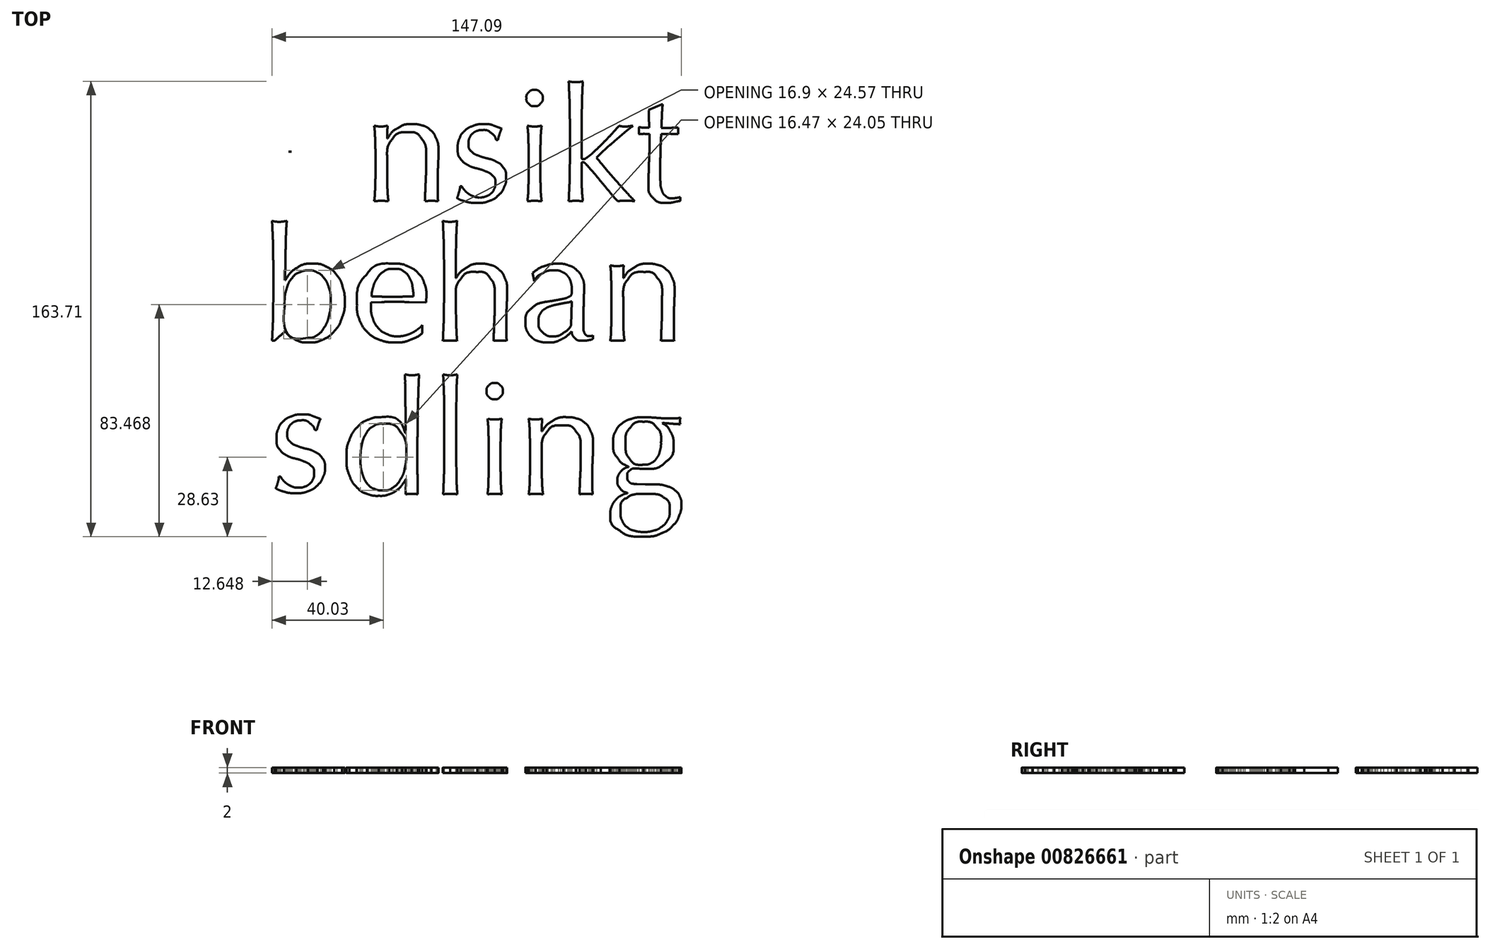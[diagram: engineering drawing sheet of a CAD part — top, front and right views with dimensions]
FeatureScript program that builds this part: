
annotation { "Feature Type Name" : "Feature", "Feature Type Description" : "" }
export const myFeature = defineFeature(function(context is Context, id is Id, definition is map)
    precondition{}
    {
        {
            var Q0;
            Q0=qCreatedBy(makeId("Top.planeOp"),FACE);
            var sketch = newSketch(context, id + "F0", { "sketchPlane" : qUnion([Q0])});
            skFitSpline(sketch, "E0", {"points": [v(-65.69, 52.86) * mm, v(-64.7, 52.86) * mm, v(-63.67, 52.84) * mm, v(-62.6, 52.8) * mm]});
            skFitSpline(sketch, "E1", {"points": [v(-62.6, 52.8) * mm, v(-61.54, 52.76) * mm, v(-60.5, 52.74) * mm, v(-59.52, 52.74) * mm]});
            skFitSpline(sketch, "E2", {"points": [v(-59.52, 52.74) * mm, v(-58.45, 52.74) * mm, v(-57.39, 52.74) * mm, v(-56.32, 52.74) * mm]});
            skFitSpline(sketch, "E3", {"points": [v(-56.32, 52.74) * mm, v(-55.25, 52.78) * mm, v(-54.19, 52.82) * mm, v(-53.12, 52.86) * mm]});
            skFitSpline(sketch, "E4", {"points": [v(-40.38, 35.08) * mm, v(-40.9, 35.16) * mm, v(-41.42, 35.2) * mm, v(-41.92, 35.2) * mm]});
            skFitSpline(sketch, "E5", {"points": [v(-41.92, 35.2) * mm, v(-42.38, 35.2) * mm, v(-42.87, 35.2) * mm, v(-43.4, 35.2) * mm]});
            skFitSpline(sketch, "E6", {"points": [v(-43.4, 35.2) * mm, v(-43.94, 35.2) * mm, v(-44.45, 35.2) * mm, v(-44.95, 35.2) * mm]});
            skFitSpline(sketch, "E7", {"points": [v(-44.95, 35.2) * mm, v(-45.4, 35.2) * mm, v(-45.9, 35.16) * mm, v(-46.43, 35.08) * mm]});
            skFitSpline(sketch, "E8", {"points": [v(-46.43, 35.08) * mm, v(-46.7, 35.96) * mm, v(-47.06, 37) * mm, v(-47.52, 38.23) * mm]});
            skFitSpline(sketch, "E9", {"points": [v(-47.52, 38.23) * mm, v(-47.98, 39.48) * mm, v(-48.49, 40.78) * mm, v(-49.06, 42.11) * mm]});
            skFitSpline(sketch, "E10", {"points": [v(-49.06, 42.11) * mm, v(-49.6, 43.48) * mm, v(-50.15, 44.86) * mm, v(-50.72, 46.23) * mm]});
            skFitSpline(sketch, "E11", {"points": [v(-50.72, 46.23) * mm, v(-51.29, 47.64) * mm, v(-51.82, 48.97) * mm, v(-52.32, 50.23) * mm]});
            skFitSpline(sketch, "E12", {"points": [v(-52.32, 50.23) * mm, v(-53.54, 50.27) * mm, v(-54.78, 50.28) * mm, v(-56.03, 50.28) * mm]});
            skFitSpline(sketch, "E13", {"points": [v(-56.03, 50.28) * mm, v(-57.29, 50.32) * mm, v(-58.55, 50.34) * mm, v(-59.8, 50.34) * mm]});
            skFitSpline(sketch, "E14", {"points": [v(-59.8, 50.34) * mm, v(-60.99, 50.34) * mm, v(-62.15, 50.32) * mm, v(-63.29, 50.28) * mm]});
            skFitSpline(sketch, "E15", {"points": [v(-63.29, 50.28) * mm, v(-64.43, 50.28) * mm, v(-65.6, 50.27) * mm, v(-66.78, 50.23) * mm]});
            skFitSpline(sketch, "E16", {"points": [v(-66.78, 50.23) * mm, v(-68, 47.26) * mm, v(-69.1, 44.42) * mm, v(-70.09, 41.71) * mm]});
            skFitSpline(sketch, "E17", {"points": [v(-70.09, 41.71) * mm, v(-71.08, 39.05) * mm, v(-71.82, 36.84) * mm, v(-72.32, 35.08) * mm]});
            skFitSpline(sketch, "E18", {"points": [v(-72.32, 35.08) * mm, v(-72.97, 35.16) * mm, v(-73.67, 35.2) * mm, v(-74.43, 35.2) * mm]});
            skFitSpline(sketch, "E19", {"points": [v(-74.43, 35.2) * mm, v(-75.2, 35.2) * mm, v(-75.9, 35.16) * mm, v(-76.55, 35.08) * mm]});
            skFitSpline(sketch, "E20", {"points": [v(-76.55, 35.08) * mm, v(-73.46, 41.75) * mm, v(-70.45, 48.38) * mm, v(-67.52, 54.97) * mm]});
            skFitSpline(sketch, "E21", {"points": [v(-67.52, 54.97) * mm, v(-64.59, 61.56) * mm, v(-61.63, 68.27) * mm, v(-58.66, 75.08) * mm]});
            skLineSegment(sketch, "E22", {"start": v(-53.12, 52.86) * mm, "end": v(-59.46, 67.37) * mm});
            skLineSegment(sketch, "E23", {"start": v(-59.46, 67.37) * mm, "end": v(-65.69, 52.86) * mm});
            skLineSegment(sketch, "E24", {"start": v(-65.69, 52.86) * mm, "end": v(-53.12, 52.86) * mm});
            skFitSpline(sketch, "E25", {"points": [v(-57.58, 75.08) * mm, v(-56.66, 72.88) * mm, v(-55.67, 70.48) * mm, v(-54.6, 67.88) * mm]});
            skFitSpline(sketch, "E26", {"points": [v(-54.6, 67.88) * mm, v(-53.54, 65.33) * mm, v(-52.45, 62.74) * mm, v(-51.35, 60.11) * mm]});
            skFitSpline(sketch, "E27", {"points": [v(-51.35, 60.11) * mm, v(-50.24, 57.48) * mm, v(-49.14, 54.88) * mm, v(-48.03, 52.28) * mm]});
            skFitSpline(sketch, "E28", {"points": [v(-48.03, 52.28) * mm, v(-46.93, 49.7) * mm, v(-45.9, 47.28) * mm, v(-44.95, 45.03) * mm]});
            skFitSpline(sketch, "E29", {"points": [v(-44.95, 45.03) * mm, v(-43.96, 42.82) * mm, v(-43.08, 40.84) * mm, v(-42.32, 39.08) * mm]});
            skFitSpline(sketch, "E30", {"points": [v(-42.32, 39.08) * mm, v(-41.52, 37.33) * mm, v(-40.87, 36) * mm, v(-40.38, 35.08) * mm]});
            skLineSegment(sketch, "E31", {"start": v(-58.66, 75.08) * mm, "end": v(-57.58, 75.08) * mm});
            skLineSegment(sketch, "E32", {"start": v(-57.58, 75.08) * mm, "end": v(-58.66, 75.08) * mm});
            skFitSpline(sketch, "E33", {"points": [v(-16.38, 47.66) * mm, v(-16.38, 45.45) * mm, v(-16.43, 43.3) * mm, v(-16.55, 41.2) * mm]});
            skFitSpline(sketch, "E34", {"points": [v(-16.55, 41.2) * mm, v(-16.62, 39.1) * mm, v(-16.7, 37.07) * mm, v(-16.78, 35.08) * mm]});
            skFitSpline(sketch, "E35", {"points": [v(-16.78, 35.08) * mm, v(-16.02, 35.16) * mm, v(-15.23, 35.2) * mm, v(-14.43, 35.2) * mm]});
            skFitSpline(sketch, "E36", {"points": [v(-14.43, 35.2) * mm, v(-13.6, 35.2) * mm, v(-12.8, 35.16) * mm, v(-12.03, 35.08) * mm]});
            skFitSpline(sketch, "E37", {"points": [v(-12.03, 35.08) * mm, v(-12.07, 35.62) * mm, v(-12.11, 36.17) * mm, v(-12.15, 36.74) * mm]});
            skFitSpline(sketch, "E38", {"points": [v(-12.15, 36.74) * mm, v(-12.15, 37.35) * mm, v(-12.15, 37.96) * mm, v(-12.15, 38.57) * mm]});
            skLineSegment(sketch, "E39", {"start": v(-16.38, 51.14) * mm, "end": v(-16.38, 47.66) * mm});
            skLineSegment(sketch, "E40", {"start": v(-16.38, 47.66) * mm, "end": v(-16.38, 51.14) * mm});
            skFitSpline(sketch, "E41", {"points": [v(-12.15, 42.28) * mm, v(-12.15, 44.23) * mm, v(-12.11, 46.06) * mm, v(-12.03, 47.77) * mm]});
            skFitSpline(sketch, "E42", {"points": [v(-12.03, 47.77) * mm, v(-11.96, 49.52) * mm, v(-11.92, 51.22) * mm, v(-11.92, 52.86) * mm]});
            skFitSpline(sketch, "E43", {"points": [v(-11.92, 52.86) * mm, v(-11.92, 54.84) * mm, v(-12.2, 56.46) * mm, v(-12.78, 57.71) * mm]});
            skFitSpline(sketch, "E44", {"points": [v(-12.78, 57.71) * mm, v(-13.31, 59) * mm, v(-14.02, 60.02) * mm, v(-14.9, 60.74) * mm]});
            skFitSpline(sketch, "E45", {"points": [v(-14.9, 60.74) * mm, v(-15.77, 61.5) * mm, v(-16.76, 62.04) * mm, v(-17.86, 62.34) * mm]});
            skFitSpline(sketch, "E46", {"points": [v(-17.86, 62.34) * mm, v(-18.93, 62.65) * mm, v(-20, 62.8) * mm, v(-21.06, 62.8) * mm]});
            skFitSpline(sketch, "E47", {"points": [v(-21.06, 62.8) * mm, v(-23.12, 62.8) * mm, v(-24.9, 62.34) * mm, v(-26.38, 61.43) * mm]});
            skFitSpline(sketch, "E48", {"points": [v(-26.38, 61.43) * mm, v(-27.86, 60.55) * mm, v(-29.14, 59.3) * mm, v(-30.2, 57.66) * mm]});
            skLineSegment(sketch, "E49", {"start": v(-12.15, 38.57) * mm, "end": v(-12.15, 42.28) * mm});
            skLineSegment(sketch, "E50", {"start": v(-12.15, 42.28) * mm, "end": v(-12.15, 38.57) * mm});
            skFitSpline(sketch, "E51", {"points": [v(-30.32, 57.66) * mm, v(-30.32, 59.18) * mm, v(-30.26, 60.7) * mm, v(-30.15, 62.23) * mm]});
            skFitSpline(sketch, "E52", {"points": [v(-30.15, 62.23) * mm, v(-30.64, 62.15) * mm, v(-31.08, 62.08) * mm, v(-31.46, 62) * mm]});
            skFitSpline(sketch, "E53", {"points": [v(-31.46, 62) * mm, v(-31.8, 61.96) * mm, v(-32.13, 61.94) * mm, v(-32.43, 61.94) * mm]});
            skFitSpline(sketch, "E54", {"points": [v(-32.43, 61.94) * mm, v(-33.08, 61.94) * mm, v(-33.94, 62.04) * mm, v(-35, 62.23) * mm]});
            skFitSpline(sketch, "E55", {"points": [v(-35, 62.23) * mm, v(-34.82, 60.59) * mm, v(-34.7, 58.82) * mm, v(-34.66, 56.91) * mm]});
            skFitSpline(sketch, "E56", {"points": [v(-34.66, 56.91) * mm, v(-34.59, 55.05) * mm, v(-34.55, 53.26) * mm, v(-34.55, 51.54) * mm]});
            skLineSegment(sketch, "E57", {"start": v(-30.2, 57.66) * mm, "end": v(-30.32, 57.66) * mm});
            skLineSegment(sketch, "E58", {"start": v(-30.32, 57.66) * mm, "end": v(-30.2, 57.66) * mm});
            skFitSpline(sketch, "E59", {"points": [v(-34.55, 45.6) * mm, v(-34.55, 43.88) * mm, v(-34.59, 42.08) * mm, v(-34.66, 40.17) * mm]});
            skFitSpline(sketch, "E60", {"points": [v(-34.66, 40.17) * mm, v(-34.7, 38.3) * mm, v(-34.82, 36.6) * mm, v(-35, 35.08) * mm]});
            skFitSpline(sketch, "E61", {"points": [v(-35, 35.08) * mm, v(-34.13, 35.16) * mm, v(-33.27, 35.2) * mm, v(-32.43, 35.2) * mm]});
            skFitSpline(sketch, "E62", {"points": [v(-32.43, 35.2) * mm, v(-31.6, 35.2) * mm, v(-30.74, 35.16) * mm, v(-29.86, 35.08) * mm]});
            skFitSpline(sketch, "E63", {"points": [v(-29.86, 35.08) * mm, v(-30.05, 36.6) * mm, v(-30.19, 38.3) * mm, v(-30.26, 40.17) * mm]});
            skFitSpline(sketch, "E64", {"points": [v(-30.26, 40.17) * mm, v(-30.3, 42.08) * mm, v(-30.32, 43.88) * mm, v(-30.32, 45.6) * mm]});
            skLineSegment(sketch, "E65", {"start": v(-34.55, 51.54) * mm, "end": v(-34.55, 45.6) * mm});
            skLineSegment(sketch, "E66", {"start": v(-34.55, 45.6) * mm, "end": v(-34.55, 51.54) * mm});
            skFitSpline(sketch, "E67", {"points": [v(-30.32, 50.46) * mm, v(-30.32, 53.43) * mm, v(-29.71, 55.73) * mm, v(-28.5, 57.37) * mm]});
            skFitSpline(sketch, "E68", {"points": [v(-28.5, 57.37) * mm, v(-27.23, 59) * mm, v(-25.27, 59.83) * mm, v(-22.6, 59.83) * mm]});
            skFitSpline(sketch, "E69", {"points": [v(-22.6, 59.83) * mm, v(-20.66, 59.83) * mm, v(-19.14, 59.08) * mm, v(-18.03, 57.6) * mm]});
            skFitSpline(sketch, "E70", {"points": [v(-18.03, 57.6) * mm, v(-16.93, 56.15) * mm, v(-16.38, 54) * mm, v(-16.38, 51.14) * mm]});
            skLineSegment(sketch, "E71", {"start": v(-30.32, 45.6) * mm, "end": v(-30.32, 50.46) * mm});
            skLineSegment(sketch, "E72", {"start": v(-30.32, 50.46) * mm, "end": v(-30.32, 45.6) * mm});
            skFitSpline(sketch, "E73", {"points": [v(-4.17, 40.4) * mm, v(-4.17, 39.83) * mm, v(-4.3, 39.1) * mm, v(-4.57, 38.23) * mm]});
            skFitSpline(sketch, "E74", {"points": [v(-4.57, 38.23) * mm, v(-4.8, 37.39) * mm, v(-5.03, 36.72) * mm, v(-5.26, 36.23) * mm]});
            skFitSpline(sketch, "E75", {"points": [v(-5.26, 36.23) * mm, v(-4.46, 35.77) * mm, v(-3.46, 35.37) * mm, v(-2.28, 35.03) * mm]});
            skFitSpline(sketch, "E76", {"points": [v(-2.28, 35.03) * mm, v(-1.1, 34.68) * mm, v(0.36, 34.51) * mm, v(2.12, 34.51) * mm]});
            skFitSpline(sketch, "E77", {"points": [v(2.12, 34.51) * mm, v(3.72, 34.51) * mm, v(5.14, 34.74) * mm, v(6.4, 35.2) * mm]});
            skFitSpline(sketch, "E78", {"points": [v(6.4, 35.2) * mm, v(7.66, 35.7) * mm, v(8.73, 36.36) * mm, v(9.6, 37.2) * mm]});
            skFitSpline(sketch, "E79", {"points": [v(9.6, 37.2) * mm, v(10.52, 38.08) * mm, v(11.2, 39.05) * mm, v(11.66, 40.11) * mm]});
            skFitSpline(sketch, "E80", {"points": [v(11.66, 40.11) * mm, v(12.15, 41.18) * mm, v(12.4, 42.27) * mm, v(12.4, 43.37) * mm]});
            skFitSpline(sketch, "E81", {"points": [v(12.4, 43.37) * mm, v(12.4, 44.97) * mm, v(12.06, 46.23) * mm, v(11.37, 47.14) * mm]});
            skFitSpline(sketch, "E82", {"points": [v(11.37, 47.14) * mm, v(10.73, 48.06) * mm, v(9.9, 48.76) * mm, v(8.92, 49.26) * mm]});
            skFitSpline(sketch, "E83", {"points": [v(8.92, 49.26) * mm, v(7.93, 49.79) * mm, v(6.84, 50.19) * mm, v(5.66, 50.46) * mm]});
            skFitSpline(sketch, "E84", {"points": [v(5.66, 50.46) * mm, v(4.48, 50.76) * mm, v(3.4, 51.1) * mm, v(2.4, 51.48) * mm]});
            skFitSpline(sketch, "E85", {"points": [v(2.4, 51.48) * mm, v(1.41, 51.87) * mm, v(0.57, 52.38) * mm, v(-0.11, 53.03) * mm]});
            skFitSpline(sketch, "E86", {"points": [v(-0.11, 53.03) * mm, v(-0.76, 53.71) * mm, v(-1.08, 54.67) * mm, v(-1.08, 55.88) * mm]});
            skFitSpline(sketch, "E87", {"points": [v(-1.08, 55.88) * mm, v(-1.08, 56.72) * mm, v(-0.93, 57.45) * mm, v(-0.63, 58.06) * mm]});
            skFitSpline(sketch, "E88", {"points": [v(-0.63, 58.06) * mm, v(-0.32, 58.67) * mm, v(0.06, 59.16) * mm, v(0.52, 59.54) * mm]});
            skFitSpline(sketch, "E89", {"points": [v(0.52, 59.54) * mm, v(0.97, 59.92) * mm, v(1.49, 60.2) * mm, v(2.06, 60.4) * mm]});
            skFitSpline(sketch, "E90", {"points": [v(2.06, 60.4) * mm, v(2.63, 60.59) * mm, v(3.2, 60.68) * mm, v(3.77, 60.68) * mm]});
            skFitSpline(sketch, "E91", {"points": [v(3.77, 60.68) * mm, v(5.07, 60.68) * mm, v(6.15, 60.32) * mm, v(7.03, 59.6) * mm]});
            skFitSpline(sketch, "E92", {"points": [v(7.03, 59.6) * mm, v(7.9, 58.88) * mm, v(8.5, 58.06) * mm, v(8.8, 57.14) * mm]});
            skLineSegment(sketch, "E93", {"start": v(-3.48, 40.4) * mm, "end": v(-4.17, 40.4) * mm});
            skLineSegment(sketch, "E94", {"start": v(-4.17, 40.4) * mm, "end": v(-3.48, 40.4) * mm});
            skFitSpline(sketch, "E95", {"points": [v(9.49, 57.14) * mm, v(9.56, 57.6) * mm, v(9.74, 58.25) * mm, v(10, 59.08) * mm]});
            skFitSpline(sketch, "E96", {"points": [v(10, 59.08) * mm, v(10.27, 59.92) * mm, v(10.55, 60.63) * mm, v(10.86, 61.2) * mm]});
            skFitSpline(sketch, "E97", {"points": [v(10.86, 61.2) * mm, v(9.98, 61.5) * mm, v(9.05, 61.85) * mm, v(8.06, 62.23) * mm]});
            skFitSpline(sketch, "E98", {"points": [v(8.06, 62.23) * mm, v(7.1, 62.6) * mm, v(5.93, 62.8) * mm, v(4.52, 62.8) * mm]});
            skFitSpline(sketch, "E99", {"points": [v(4.52, 62.8) * mm, v(3, 62.8) * mm, v(1.64, 62.57) * mm, v(0.46, 62.11) * mm]});
            skFitSpline(sketch, "E100", {"points": [v(0.46, 62.11) * mm, v(-0.72, 61.7) * mm, v(-1.71, 61.1) * mm, v(-2.51, 60.34) * mm]});
            skFitSpline(sketch, "E101", {"points": [v(-2.51, 60.34) * mm, v(-3.31, 59.58) * mm, v(-3.92, 58.67) * mm, v(-4.34, 57.6) * mm]});
            skFitSpline(sketch, "E102", {"points": [v(-4.34, 57.6) * mm, v(-4.76, 56.57) * mm, v(-4.97, 55.43) * mm, v(-4.97, 54.17) * mm]});
            skFitSpline(sketch, "E103", {"points": [v(-4.97, 54.17) * mm, v(-4.97, 52.57) * mm, v(-4.65, 51.31) * mm, v(-4, 50.4) * mm]});
            skFitSpline(sketch, "E104", {"points": [v(-4, 50.4) * mm, v(-3.31, 49.48) * mm, v(-2.47, 48.74) * mm, v(-1.48, 48.17) * mm]});
            skFitSpline(sketch, "E105", {"points": [v(-1.48, 48.17) * mm, v(-0.5, 47.64) * mm, v(0.6, 47.22) * mm, v(1.77, 46.91) * mm]});
            skFitSpline(sketch, "E106", {"points": [v(1.77, 46.91) * mm, v(2.95, 46.6) * mm, v(4.04, 46.25) * mm, v(5.03, 45.83) * mm]});
            skFitSpline(sketch, "E107", {"points": [v(5.03, 45.83) * mm, v(6.02, 45.45) * mm, v(6.84, 44.93) * mm, v(7.49, 44.28) * mm]});
            skFitSpline(sketch, "E108", {"points": [v(7.49, 44.28) * mm, v(8.17, 43.68) * mm, v(8.52, 42.78) * mm, v(8.52, 41.6) * mm]});
            skFitSpline(sketch, "E109", {"points": [v(8.52, 41.6) * mm, v(8.52, 40.76) * mm, v(8.36, 40.02) * mm, v(8.06, 39.37) * mm]});
            skFitSpline(sketch, "E110", {"points": [v(8.06, 39.37) * mm, v(7.75, 38.72) * mm, v(7.34, 38.19) * mm, v(6.8, 37.77) * mm]});
            skFitSpline(sketch, "E111", {"points": [v(6.8, 37.77) * mm, v(6.3, 37.35) * mm, v(5.72, 37.03) * mm, v(5.03, 36.8) * mm]});
            skFitSpline(sketch, "E112", {"points": [v(5.03, 36.8) * mm, v(4.38, 36.57) * mm, v(3.7, 36.46) * mm, v(2.97, 36.46) * mm]});
            skFitSpline(sketch, "E113", {"points": [v(2.97, 36.46) * mm, v(2.17, 36.46) * mm, v(1.41, 36.59) * mm, v(0.69, 36.86) * mm]});
            skFitSpline(sketch, "E114", {"points": [v(0.69, 36.86) * mm, v(0, 37.12) * mm, v(-0.63, 37.45) * mm, v(-1.2, 37.83) * mm]});
            skFitSpline(sketch, "E115", {"points": [v(-1.2, 37.83) * mm, v(-1.73, 38.25) * mm, v(-2.2, 38.68) * mm, v(-2.63, 39.14) * mm]});
            skFitSpline(sketch, "E116", {"points": [v(-2.63, 39.14) * mm, v(-3, 39.6) * mm, v(-3.3, 40.02) * mm, v(-3.48, 40.4) * mm]});
            skLineSegment(sketch, "E117", {"start": v(8.8, 57.14) * mm, "end": v(9.49, 57.14) * mm});
            skLineSegment(sketch, "E118", {"start": v(9.49, 57.14) * mm, "end": v(8.8, 57.14) * mm});
            skFitSpline(sketch, "E119", {"points": [v(19.7, 72.17) * mm, v(19.7, 71.37) * mm, v(19.98, 70.68) * mm, v(20.55, 70.11) * mm]});
            skFitSpline(sketch, "E120", {"points": [v(20.55, 70.11) * mm, v(21.13, 69.54) * mm, v(21.81, 69.26) * mm, v(22.61, 69.26) * mm]});
            skFitSpline(sketch, "E121", {"points": [v(22.61, 69.26) * mm, v(23.41, 69.26) * mm, v(24.1, 69.54) * mm, v(24.67, 70.11) * mm]});
            skFitSpline(sketch, "E122", {"points": [v(24.67, 70.11) * mm, v(25.24, 70.68) * mm, v(25.53, 71.37) * mm, v(25.53, 72.17) * mm]});
            skFitSpline(sketch, "E123", {"points": [v(25.53, 72.17) * mm, v(25.53, 72.97) * mm, v(25.24, 73.66) * mm, v(24.67, 74.23) * mm]});
            skFitSpline(sketch, "E124", {"points": [v(24.67, 74.23) * mm, v(24.1, 74.8) * mm, v(23.41, 75.08) * mm, v(22.61, 75.08) * mm]});
            skFitSpline(sketch, "E125", {"points": [v(22.61, 75.08) * mm, v(21.81, 75.08) * mm, v(21.13, 74.8) * mm, v(20.55, 74.23) * mm]});
            skFitSpline(sketch, "E126", {"points": [v(20.55, 74.23) * mm, v(19.98, 73.66) * mm, v(19.7, 72.97) * mm, v(19.7, 72.17) * mm]});
            skFitSpline(sketch, "E127", {"points": [v(20.5, 45.6) * mm, v(20.5, 43.88) * mm, v(20.46, 42.08) * mm, v(20.38, 40.17) * mm]});
            skFitSpline(sketch, "E128", {"points": [v(20.38, 40.17) * mm, v(20.35, 38.3) * mm, v(20.23, 36.6) * mm, v(20.04, 35.08) * mm]});
            skFitSpline(sketch, "E129", {"points": [v(20.04, 35.08) * mm, v(20.92, 35.16) * mm, v(21.77, 35.2) * mm, v(22.61, 35.2) * mm]});
            skFitSpline(sketch, "E130", {"points": [v(22.61, 35.2) * mm, v(23.45, 35.2) * mm, v(24.3, 35.16) * mm, v(25.18, 35.08) * mm]});
            skFitSpline(sketch, "E131", {"points": [v(25.18, 35.08) * mm, v(25, 36.6) * mm, v(24.86, 38.3) * mm, v(24.78, 40.17) * mm]});
            skFitSpline(sketch, "E132", {"points": [v(24.78, 40.17) * mm, v(24.75, 42.08) * mm, v(24.73, 43.88) * mm, v(24.73, 45.6) * mm]});
            skLineSegment(sketch, "E133", {"start": v(20.5, 51.54) * mm, "end": v(20.5, 45.6) * mm});
            skLineSegment(sketch, "E134", {"start": v(20.5, 45.6) * mm, "end": v(20.5, 51.54) * mm});
            skFitSpline(sketch, "E135", {"points": [v(24.73, 51.54) * mm, v(24.73, 53.26) * mm, v(24.75, 55.05) * mm, v(24.78, 56.91) * mm]});
            skFitSpline(sketch, "E136", {"points": [v(24.78, 56.91) * mm, v(24.86, 58.82) * mm, v(25, 60.59) * mm, v(25.18, 62.23) * mm]});
            skFitSpline(sketch, "E137", {"points": [v(25.18, 62.23) * mm, v(24.12, 62.04) * mm, v(23.26, 61.94) * mm, v(22.61, 61.94) * mm]});
            skFitSpline(sketch, "E138", {"points": [v(22.61, 61.94) * mm, v(21.96, 61.94) * mm, v(21.1, 62.04) * mm, v(20.04, 62.23) * mm]});
            skFitSpline(sketch, "E139", {"points": [v(20.04, 62.23) * mm, v(20.23, 60.59) * mm, v(20.35, 58.82) * mm, v(20.38, 56.91) * mm]});
            skFitSpline(sketch, "E140", {"points": [v(20.38, 56.91) * mm, v(20.46, 55.05) * mm, v(20.5, 53.26) * mm, v(20.5, 51.54) * mm]});
            skLineSegment(sketch, "E141", {"start": v(24.73, 45.6) * mm, "end": v(24.73, 51.54) * mm});
            skLineSegment(sketch, "E142", {"start": v(24.73, 51.54) * mm, "end": v(24.73, 45.6) * mm});
            skFitSpline(sketch, "E143", {"points": [v(35.32, 51.37) * mm, v(35.32, 50.08) * mm, v(35.3, 48.67) * mm, v(35.26, 47.14) * mm]});
            skFitSpline(sketch, "E144", {"points": [v(35.26, 47.14) * mm, v(35.26, 45.62) * mm, v(35.24, 44.11) * mm, v(35.2, 42.63) * mm]});
            skFitSpline(sketch, "E145", {"points": [v(35.2, 42.63) * mm, v(35.16, 41.14) * mm, v(35.1, 39.73) * mm, v(35.03, 38.4) * mm]});
            skFitSpline(sketch, "E146", {"points": [v(35.03, 38.4) * mm, v(35, 37.07) * mm, v(34.94, 35.96) * mm, v(34.86, 35.08) * mm]});
            skFitSpline(sketch, "E147", {"points": [v(34.86, 35.08) * mm, v(35.74, 35.16) * mm, v(36.6, 35.2) * mm, v(37.43, 35.2) * mm]});
            skFitSpline(sketch, "E148", {"points": [v(37.43, 35.2) * mm, v(38.27, 35.2) * mm, v(39.13, 35.16) * mm, v(40, 35.08) * mm]});
            skFitSpline(sketch, "E149", {"points": [v(40, 35.08) * mm, v(39.81, 36.72) * mm, v(39.68, 38.34) * mm, v(39.6, 39.94) * mm]});
            skFitSpline(sketch, "E150", {"points": [v(39.6, 39.94) * mm, v(39.56, 41.58) * mm, v(39.55, 43.26) * mm, v(39.55, 44.97) * mm]});
            skLineSegment(sketch, "E151", {"start": v(35.32, 61.71) * mm, "end": v(35.32, 51.37) * mm});
            skLineSegment(sketch, "E152", {"start": v(35.32, 51.37) * mm, "end": v(35.32, 61.71) * mm});
            skFitSpline(sketch, "E153", {"points": [v(39.55, 48.4) * mm, v(39.55, 48.86) * mm, v(39.74, 49.08) * mm, v(40.12, 49.08) * mm]});
            skFitSpline(sketch, "E154", {"points": [v(40.12, 49.08) * mm, v(40.27, 49.08) * mm, v(40.42, 49.03) * mm, v(40.57, 48.91) * mm]});
            skFitSpline(sketch, "E155", {"points": [v(40.57, 48.91) * mm, v(40.73, 48.8) * mm, v(40.86, 48.67) * mm, v(40.97, 48.51) * mm]});
            skFitSpline(sketch, "E156", {"points": [v(40.97, 48.51) * mm, v(41.66, 47.79) * mm, v(42.48, 46.88) * mm, v(43.43, 45.77) * mm]});
            skFitSpline(sketch, "E157", {"points": [v(43.43, 45.77) * mm, v(44.38, 44.67) * mm, v(45.37, 43.48) * mm, v(46.4, 42.23) * mm]});
            skFitSpline(sketch, "E158", {"points": [v(46.4, 42.23) * mm, v(47.47, 40.97) * mm, v(48.54, 39.7) * mm, v(49.6, 38.4) * mm]});
            skFitSpline(sketch, "E159", {"points": [v(49.6, 38.4) * mm, v(50.67, 37.14) * mm, v(51.62, 36.04) * mm, v(52.46, 35.08) * mm]});
            skFitSpline(sketch, "E160", {"points": [v(52.46, 35.08) * mm, v(53, 35.16) * mm, v(53.5, 35.2) * mm, v(54, 35.2) * mm]});
            skFitSpline(sketch, "E161", {"points": [v(54, 35.2) * mm, v(54.5, 35.2) * mm, v(54.96, 35.2) * mm, v(55.37, 35.2) * mm]});
            skFitSpline(sketch, "E162", {"points": [v(55.37, 35.2) * mm, v(55.87, 35.2) * mm, v(56.36, 35.2) * mm, v(56.86, 35.2) * mm]});
            skFitSpline(sketch, "E163", {"points": [v(56.86, 35.2) * mm, v(57.4, 35.2) * mm, v(57.98, 35.16) * mm, v(58.63, 35.08) * mm]});
            skFitSpline(sketch, "E164", {"points": [v(58.63, 35.08) * mm, v(56.23, 37.64) * mm, v(53.87, 40.23) * mm, v(51.55, 42.86) * mm]});
            skFitSpline(sketch, "E165", {"points": [v(51.55, 42.86) * mm, v(49.26, 45.48) * mm, v(47.03, 48.11) * mm, v(44.86, 50.74) * mm]});
            skFitSpline(sketch, "E166", {"points": [v(44.86, 50.74) * mm, v(46.84, 52.68) * mm, v(48.92, 54.59) * mm, v(51.09, 56.46) * mm]});
            skFitSpline(sketch, "E167", {"points": [v(51.09, 56.46) * mm, v(53.3, 58.36) * mm, v(55.6, 60.28) * mm, v(58, 62.23) * mm]});
            skFitSpline(sketch, "E168", {"points": [v(58, 62.23) * mm, v(57.36, 62.15) * mm, v(56.82, 62.08) * mm, v(56.4, 62) * mm]});
            skFitSpline(sketch, "E169", {"points": [v(56.4, 62) * mm, v(55.98, 61.96) * mm, v(55.56, 61.94) * mm, v(55.15, 61.94) * mm]});
            skFitSpline(sketch, "E170", {"points": [v(55.15, 61.94) * mm, v(54.46, 61.94) * mm, v(53.74, 62.04) * mm, v(52.97, 62.23) * mm]});
            skFitSpline(sketch, "E171", {"points": [v(52.97, 62.23) * mm, v(52.1, 61.2) * mm, v(51.13, 60.11) * mm, v(50.06, 58.97) * mm]});
            skFitSpline(sketch, "E172", {"points": [v(50.06, 58.97) * mm, v(49, 57.83) * mm, v(47.95, 56.74) * mm, v(46.92, 55.71) * mm]});
            skFitSpline(sketch, "E173", {"points": [v(46.92, 55.71) * mm, v(45.93, 54.72) * mm, v(45.01, 53.85) * mm, v(44.17, 53.08) * mm]});
            skFitSpline(sketch, "E174", {"points": [v(44.17, 53.08) * mm, v(43.37, 52.32) * mm, v(42.8, 51.8) * mm, v(42.46, 51.54) * mm]});
            skFitSpline(sketch, "E175", {"points": [v(42.46, 51.54) * mm, v(42, 51.2) * mm, v(41.58, 50.9) * mm, v(41.2, 50.63) * mm]});
            skFitSpline(sketch, "E176", {"points": [v(41.2, 50.63) * mm, v(40.86, 50.36) * mm, v(40.54, 50.23) * mm, v(40.23, 50.23) * mm]});
            skFitSpline(sketch, "E177", {"points": [v(40.23, 50.23) * mm, v(39.77, 50.23) * mm, v(39.55, 50.59) * mm, v(39.55, 51.31) * mm]});
            skLineSegment(sketch, "E178", {"start": v(39.55, 44.97) * mm, "end": v(39.55, 48.4) * mm});
            skLineSegment(sketch, "E179", {"start": v(39.55, 48.4) * mm, "end": v(39.55, 44.97) * mm});
            skFitSpline(sketch, "E180", {"points": [v(39.55, 61.71) * mm, v(39.55, 63) * mm, v(39.55, 64.42) * mm, v(39.55, 65.94) * mm]});
            skFitSpline(sketch, "E181", {"points": [v(39.55, 65.94) * mm, v(39.58, 67.47) * mm, v(39.62, 68.97) * mm, v(39.66, 70.46) * mm]});
            skFitSpline(sketch, "E182", {"points": [v(39.66, 70.46) * mm, v(39.7, 71.94) * mm, v(39.74, 73.35) * mm, v(39.77, 74.68) * mm]});
            skFitSpline(sketch, "E183", {"points": [v(39.77, 74.68) * mm, v(39.85, 76.06) * mm, v(39.93, 77.22) * mm, v(40, 78.17) * mm]});
            skFitSpline(sketch, "E184", {"points": [v(40, 78.17) * mm, v(38.94, 77.98) * mm, v(38.08, 77.88) * mm, v(37.43, 77.88) * mm]});
            skFitSpline(sketch, "E185", {"points": [v(37.43, 77.88) * mm, v(36.78, 77.88) * mm, v(35.93, 77.98) * mm, v(34.86, 78.17) * mm]});
            skFitSpline(sketch, "E186", {"points": [v(34.86, 78.17) * mm, v(34.94, 77.22) * mm, v(35, 76.06) * mm, v(35.03, 74.68) * mm]});
            skFitSpline(sketch, "E187", {"points": [v(35.03, 74.68) * mm, v(35.1, 73.35) * mm, v(35.16, 71.94) * mm, v(35.2, 70.46) * mm]});
            skFitSpline(sketch, "E188", {"points": [v(35.2, 70.46) * mm, v(35.24, 68.97) * mm, v(35.26, 67.47) * mm, v(35.26, 65.94) * mm]});
            skFitSpline(sketch, "E189", {"points": [v(35.26, 65.94) * mm, v(35.3, 64.42) * mm, v(35.32, 63) * mm, v(35.32, 61.71) * mm]});
            skLineSegment(sketch, "E190", {"start": v(39.55, 51.31) * mm, "end": v(39.55, 61.71) * mm});
            skLineSegment(sketch, "E191", {"start": v(39.55, 61.71) * mm, "end": v(39.55, 51.31) * mm});
            skFitSpline(sketch, "E192", {"points": [v(63.6, 67.88) * mm, v(63.68, 66.67) * mm, v(63.72, 65.48) * mm, v(63.72, 64.34) * mm]});
            skFitSpline(sketch, "E193", {"points": [v(63.72, 64.34) * mm, v(63.76, 63.2) * mm, v(63.8, 62.25) * mm, v(63.83, 61.48) * mm]});
            skFitSpline(sketch, "E194", {"points": [v(63.83, 61.48) * mm, v(63.03, 61.48) * mm, v(61.77, 61.54) * mm, v(60.06, 61.66) * mm]});
            skFitSpline(sketch, "E195", {"points": [v(60.06, 61.66) * mm, v(60.1, 61.47) * mm, v(60.12, 61.28) * mm, v(60.12, 61.08) * mm]});
            skFitSpline(sketch, "E196", {"points": [v(60.12, 61.08) * mm, v(60.16, 60.9) * mm, v(60.17, 60.7) * mm, v(60.17, 60.51) * mm]});
            skFitSpline(sketch, "E197", {"points": [v(60.17, 60.51) * mm, v(60.17, 60.28) * mm, v(60.16, 60.06) * mm, v(60.12, 59.83) * mm]});
            skFitSpline(sketch, "E198", {"points": [v(60.12, 59.83) * mm, v(60.12, 59.64) * mm, v(60.1, 59.43) * mm, v(60.06, 59.2) * mm]});
            skFitSpline(sketch, "E199", {"points": [v(60.06, 59.2) * mm, v(60.44, 59.24) * mm, v(60.8, 59.26) * mm, v(61.15, 59.26) * mm]});
            skFitSpline(sketch, "E200", {"points": [v(61.15, 59.26) * mm, v(61.49, 59.3) * mm, v(61.81, 59.31) * mm, v(62.12, 59.31) * mm]});
            skLineSegment(sketch, "E201", {"start": v(68.35, 69.88) * mm, "end": v(63.6, 67.88) * mm});
            skLineSegment(sketch, "E202", {"start": v(63.6, 67.88) * mm, "end": v(68.35, 69.88) * mm});
            skFitSpline(sketch, "E203", {"points": [v(63.95, 59.31) * mm, v(63.95, 57.18) * mm, v(63.93, 55.24) * mm, v(63.89, 53.48) * mm]});
            skFitSpline(sketch, "E204", {"points": [v(63.89, 53.48) * mm, v(63.85, 51.77) * mm, v(63.8, 50.19) * mm, v(63.72, 48.74) * mm]});
            skFitSpline(sketch, "E205", {"points": [v(63.72, 48.74) * mm, v(63.68, 47.33) * mm, v(63.64, 46.02) * mm, v(63.6, 44.8) * mm]});
            skFitSpline(sketch, "E206", {"points": [v(63.6, 44.8) * mm, v(63.56, 43.62) * mm, v(63.55, 42.51) * mm, v(63.55, 41.48) * mm]});
            skFitSpline(sketch, "E207", {"points": [v(63.55, 41.48) * mm, v(63.55, 39.2) * mm, v(64.12, 37.47) * mm, v(65.26, 36.28) * mm]});
            skFitSpline(sketch, "E208", {"points": [v(65.26, 36.28) * mm, v(66.4, 35.1) * mm, v(68.17, 34.51) * mm, v(70.57, 34.51) * mm]});
            skFitSpline(sketch, "E209", {"points": [v(70.57, 34.51) * mm, v(71.3, 34.51) * mm, v(72.04, 34.6) * mm, v(72.8, 34.8) * mm]});
            skFitSpline(sketch, "E210", {"points": [v(72.8, 34.8) * mm, v(73.6, 34.95) * mm, v(74.33, 35.08) * mm, v(74.97, 35.2) * mm]});
            skLineSegment(sketch, "E211", {"start": v(62.12, 59.31) * mm, "end": v(63.95, 59.31) * mm});
            skLineSegment(sketch, "E212", {"start": v(63.95, 59.31) * mm, "end": v(62.12, 59.31) * mm});
            skFitSpline(sketch, "E213", {"points": [v(74.97, 36.57) * mm, v(74.6, 36.46) * mm, v(74.14, 36.36) * mm, v(73.6, 36.28) * mm]});
            skFitSpline(sketch, "E214", {"points": [v(73.6, 36.28) * mm, v(73.1, 36.2) * mm, v(72.7, 36.17) * mm, v(72.4, 36.17) * mm]});
            skFitSpline(sketch, "E215", {"points": [v(72.4, 36.17) * mm, v(71.26, 36.17) * mm, v(70.38, 36.42) * mm, v(69.77, 36.91) * mm]});
            skFitSpline(sketch, "E216", {"points": [v(69.77, 36.91) * mm, v(69.16, 37.4) * mm, v(68.7, 38.06) * mm, v(68.4, 38.86) * mm]});
            skFitSpline(sketch, "E217", {"points": [v(68.4, 38.86) * mm, v(68.1, 39.7) * mm, v(67.9, 40.63) * mm, v(67.83, 41.66) * mm]});
            skFitSpline(sketch, "E218", {"points": [v(67.83, 41.66) * mm, v(67.8, 42.68) * mm, v(67.77, 43.73) * mm, v(67.77, 44.8) * mm]});
            skFitSpline(sketch, "E219", {"points": [v(67.77, 44.8) * mm, v(67.77, 46.06) * mm, v(67.77, 47.48) * mm, v(67.77, 49.08) * mm]});
            skFitSpline(sketch, "E220", {"points": [v(67.77, 49.08) * mm, v(67.81, 50.68) * mm, v(67.85, 52.2) * mm, v(67.89, 53.66) * mm]});
            skFitSpline(sketch, "E221", {"points": [v(67.89, 53.66) * mm, v(67.93, 55.14) * mm, v(67.96, 56.42) * mm, v(68, 57.48) * mm]});
            skFitSpline(sketch, "E222", {"points": [v(68, 57.48) * mm, v(68.08, 58.55) * mm, v(68.14, 59.16) * mm, v(68.17, 59.31) * mm]});
            skLineSegment(sketch, "E223", {"start": v(74.97, 35.2) * mm, "end": v(74.97, 36.57) * mm});
            skLineSegment(sketch, "E224", {"start": v(74.97, 36.57) * mm, "end": v(74.97, 35.2) * mm});
            skFitSpline(sketch, "E225", {"points": [v(70.97, 59.31) * mm, v(71.58, 59.31) * mm, v(72.16, 59.3) * mm, v(72.69, 59.26) * mm]});
            skFitSpline(sketch, "E226", {"points": [v(72.69, 59.26) * mm, v(73.22, 59.26) * mm, v(73.74, 59.24) * mm, v(74.23, 59.2) * mm]});
            skFitSpline(sketch, "E227", {"points": [v(74.23, 59.2) * mm, v(74.2, 59.31) * mm, v(74.17, 59.5) * mm, v(74.17, 59.77) * mm]});
            skLineSegment(sketch, "E228", {"start": v(68.17, 59.31) * mm, "end": v(70.97, 59.31) * mm});
            skLineSegment(sketch, "E229", {"start": v(70.97, 59.31) * mm, "end": v(68.17, 59.31) * mm});
            skFitSpline(sketch, "E230", {"points": [v(74.17, 60.97) * mm, v(74.17, 61.28) * mm, v(74.2, 61.48) * mm, v(74.23, 61.6) * mm]});
            skFitSpline(sketch, "E231", {"points": [v(74.23, 61.6) * mm, v(72.9, 61.52) * mm, v(71.66, 61.47) * mm, v(70.52, 61.43) * mm]});
            skFitSpline(sketch, "E232", {"points": [v(70.52, 61.43) * mm, v(69.37, 61.43) * mm, v(68.6, 61.43) * mm, v(68.17, 61.43) * mm]});
            skFitSpline(sketch, "E233", {"points": [v(68.17, 61.43) * mm, v(68.25, 62.84) * mm, v(68.3, 64.23) * mm, v(68.35, 65.6) * mm]});
            skFitSpline(sketch, "E234", {"points": [v(68.35, 65.6) * mm, v(68.42, 67) * mm, v(68.52, 68.44) * mm, v(68.63, 69.88) * mm]});
            skLineSegment(sketch, "E235", {"start": v(74.17, 59.77) * mm, "end": v(74.17, 60.4) * mm});
            skLineSegment(sketch, "E236", {"start": v(74.17, 60.4) * mm, "end": v(74.17, 60.97) * mm});
            skLineSegment(sketch, "E237", {"start": v(74.17, 60.97) * mm, "end": v(74.17, 59.77) * mm});
            skLineSegment(sketch, "E238", {"start": v(68.63, 69.88) * mm, "end": v(68.35, 69.88) * mm});
            skLineSegment(sketch, "E239", {"start": v(68.35, 69.88) * mm, "end": v(68.63, 69.88) * mm});
            skFitSpline(sketch, "E240", {"points": [v(-69.27, -63.98) * mm, v(-69.27, -64.55) * mm, v(-69.4, -65.27) * mm, v(-69.67, -66.15) * mm]});
            skFitSpline(sketch, "E241", {"points": [v(-69.67, -66.15) * mm, v(-69.9, -66.99) * mm, v(-70.13, -67.66) * mm, v(-70.36, -68.15) * mm]});
            skFitSpline(sketch, "E242", {"points": [v(-70.36, -68.15) * mm, v(-69.56, -68.6) * mm, v(-68.57, -69) * mm, v(-67.39, -69.35) * mm]});
            skFitSpline(sketch, "E243", {"points": [v(-67.39, -69.35) * mm, v(-66.2, -69.7) * mm, v(-64.74, -69.87) * mm, v(-62.99, -69.87) * mm]});
            skFitSpline(sketch, "E244", {"points": [v(-62.99, -69.87) * mm, v(-61.39, -69.87) * mm, v(-59.96, -69.64) * mm, v(-58.7, -69.18) * mm]});
            skFitSpline(sketch, "E245", {"points": [v(-58.7, -69.18) * mm, v(-57.44, -68.68) * mm, v(-56.38, -68.02) * mm, v(-55.5, -67.18) * mm]});
            skFitSpline(sketch, "E246", {"points": [v(-55.5, -67.18) * mm, v(-54.59, -66.3) * mm, v(-53.9, -65.33) * mm, v(-53.44, -64.27) * mm]});
            skFitSpline(sketch, "E247", {"points": [v(-53.44, -64.27) * mm, v(-52.95, -63.2) * mm, v(-52.7, -62.11) * mm, v(-52.7, -61) * mm]});
            skFitSpline(sketch, "E248", {"points": [v(-52.7, -61) * mm, v(-52.7, -59.4) * mm, v(-53.04, -58.15) * mm, v(-53.73, -57.24) * mm]});
            skFitSpline(sketch, "E249", {"points": [v(-53.73, -57.24) * mm, v(-54.38, -56.32) * mm, v(-55.2, -55.62) * mm, v(-56.19, -55.12) * mm]});
            skFitSpline(sketch, "E250", {"points": [v(-56.19, -55.12) * mm, v(-57.18, -54.59) * mm, v(-58.26, -54.19) * mm, v(-59.44, -53.92) * mm]});
            skFitSpline(sketch, "E251", {"points": [v(-59.44, -53.92) * mm, v(-60.62, -53.62) * mm, v(-61.7, -53.27) * mm, v(-62.7, -52.9) * mm]});
            skFitSpline(sketch, "E252", {"points": [v(-62.7, -52.9) * mm, v(-63.69, -52.51) * mm, v(-64.53, -52) * mm, v(-65.21, -51.35) * mm]});
            skFitSpline(sketch, "E253", {"points": [v(-65.21, -51.35) * mm, v(-65.86, -50.67) * mm, v(-66.19, -49.71) * mm, v(-66.19, -48.5) * mm]});
            skFitSpline(sketch, "E254", {"points": [v(-66.19, -48.5) * mm, v(-66.19, -47.66) * mm, v(-66.03, -46.93) * mm, v(-65.73, -46.32) * mm]});
            skFitSpline(sketch, "E255", {"points": [v(-65.73, -46.32) * mm, v(-65.42, -45.71) * mm, v(-65.04, -45.22) * mm, v(-64.59, -44.84) * mm]});
            skFitSpline(sketch, "E256", {"points": [v(-64.59, -44.84) * mm, v(-64.13, -44.46) * mm, v(-63.61, -44.17) * mm, v(-63.04, -43.98) * mm]});
            skFitSpline(sketch, "E257", {"points": [v(-63.04, -43.98) * mm, v(-62.47, -43.79) * mm, v(-61.9, -43.7) * mm, v(-61.33, -43.7) * mm]});
            skFitSpline(sketch, "E258", {"points": [v(-61.33, -43.7) * mm, v(-60.03, -43.7) * mm, v(-58.95, -44.06) * mm, v(-58.07, -44.78) * mm]});
            skFitSpline(sketch, "E259", {"points": [v(-58.07, -44.78) * mm, v(-57.2, -45.5) * mm, v(-56.6, -46.32) * mm, v(-56.3, -47.24) * mm]});
            skLineSegment(sketch, "E260", {"start": v(-68.59, -63.98) * mm, "end": v(-69.27, -63.98) * mm});
            skLineSegment(sketch, "E261", {"start": v(-69.27, -63.98) * mm, "end": v(-68.59, -63.98) * mm});
            skFitSpline(sketch, "E262", {"points": [v(-55.61, -47.24) * mm, v(-55.54, -46.78) * mm, v(-55.37, -46.13) * mm, v(-55.1, -45.3) * mm]});
            skFitSpline(sketch, "E263", {"points": [v(-55.1, -45.3) * mm, v(-54.83, -44.46) * mm, v(-54.55, -43.75) * mm, v(-54.24, -43.18) * mm]});
            skFitSpline(sketch, "E264", {"points": [v(-54.24, -43.18) * mm, v(-55.12, -42.87) * mm, v(-56.05, -42.53) * mm, v(-57.04, -42.15) * mm]});
            skFitSpline(sketch, "E265", {"points": [v(-57.04, -42.15) * mm, v(-58, -41.77) * mm, v(-59.18, -41.58) * mm, v(-60.59, -41.58) * mm]});
            skFitSpline(sketch, "E266", {"points": [v(-60.59, -41.58) * mm, v(-62.1, -41.58) * mm, v(-63.46, -41.8) * mm, v(-64.64, -42.27) * mm]});
            skFitSpline(sketch, "E267", {"points": [v(-64.64, -42.27) * mm, v(-65.82, -42.68) * mm, v(-66.81, -43.27) * mm, v(-67.61, -44.04) * mm]});
            skFitSpline(sketch, "E268", {"points": [v(-67.61, -44.04) * mm, v(-68.41, -44.8) * mm, v(-69.02, -45.71) * mm, v(-69.44, -46.78) * mm]});
            skFitSpline(sketch, "E269", {"points": [v(-69.44, -46.78) * mm, v(-69.86, -47.8) * mm, v(-70.07, -48.95) * mm, v(-70.07, -50.2) * mm]});
            skFitSpline(sketch, "E270", {"points": [v(-70.07, -50.2) * mm, v(-70.07, -51.8) * mm, v(-69.75, -53.07) * mm, v(-69.1, -53.98) * mm]});
            skFitSpline(sketch, "E271", {"points": [v(-69.1, -53.98) * mm, v(-68.41, -54.9) * mm, v(-67.58, -55.64) * mm, v(-66.59, -56.2) * mm]});
            skFitSpline(sketch, "E272", {"points": [v(-66.59, -56.2) * mm, v(-65.6, -56.74) * mm, v(-64.5, -57.16) * mm, v(-63.33, -57.47) * mm]});
            skFitSpline(sketch, "E273", {"points": [v(-63.33, -57.47) * mm, v(-62.15, -57.77) * mm, v(-61.06, -58.13) * mm, v(-60.07, -58.55) * mm]});
            skFitSpline(sketch, "E274", {"points": [v(-60.07, -58.55) * mm, v(-59.08, -58.93) * mm, v(-58.26, -59.45) * mm, v(-57.61, -60.1) * mm]});
            skFitSpline(sketch, "E275", {"points": [v(-57.61, -60.1) * mm, v(-56.93, -60.7) * mm, v(-56.59, -61.6) * mm, v(-56.59, -62.78) * mm]});
            skFitSpline(sketch, "E276", {"points": [v(-56.59, -62.78) * mm, v(-56.59, -63.62) * mm, v(-56.74, -64.36) * mm, v(-57.04, -65) * mm]});
            skFitSpline(sketch, "E277", {"points": [v(-57.04, -65) * mm, v(-57.35, -65.66) * mm, v(-57.77, -66.19) * mm, v(-58.3, -66.6) * mm]});
            skFitSpline(sketch, "E278", {"points": [v(-58.3, -66.6) * mm, v(-58.8, -67.03) * mm, v(-59.39, -67.35) * mm, v(-60.07, -67.58) * mm]});
            skFitSpline(sketch, "E279", {"points": [v(-60.07, -67.58) * mm, v(-60.72, -67.8) * mm, v(-61.4, -67.92) * mm, v(-62.13, -67.92) * mm]});
            skFitSpline(sketch, "E280", {"points": [v(-62.13, -67.92) * mm, v(-62.93, -67.92) * mm, v(-63.69, -67.79) * mm, v(-64.41, -67.52) * mm]});
            skFitSpline(sketch, "E281", {"points": [v(-64.41, -67.52) * mm, v(-65.1, -67.26) * mm, v(-65.73, -66.93) * mm, v(-66.3, -66.55) * mm]});
            skFitSpline(sketch, "E282", {"points": [v(-66.3, -66.55) * mm, v(-66.83, -66.13) * mm, v(-67.3, -65.7) * mm, v(-67.73, -65.24) * mm]});
            skFitSpline(sketch, "E283", {"points": [v(-67.73, -65.24) * mm, v(-68.1, -64.78) * mm, v(-68.4, -64.36) * mm, v(-68.59, -63.98) * mm]});
            skLineSegment(sketch, "E284", {"start": v(-56.3, -47.24) * mm, "end": v(-55.61, -47.24) * mm});
            skLineSegment(sketch, "E285", {"start": v(-55.61, -47.24) * mm, "end": v(-56.3, -47.24) * mm});
            skFitSpline(sketch, "E286", {"points": [v(-50.62, -0.66) * mm, v(-50.62, -2.68) * mm, v(-50.83, -4.5) * mm, v(-51.25, -6.15) * mm]});
            skFitSpline(sketch, "E287", {"points": [v(-51.25, -6.15) * mm, v(-51.67, -7.78) * mm, v(-52.26, -9.2) * mm, v(-53.02, -10.37) * mm]});
            skFitSpline(sketch, "E288", {"points": [v(-53.02, -10.37) * mm, v(-53.74, -11.55) * mm, v(-54.6, -12.47) * mm, v(-55.6, -13.12) * mm]});
            skFitSpline(sketch, "E289", {"points": [v(-55.6, -13.12) * mm, v(-56.58, -13.73) * mm, v(-57.67, -14.03) * mm, v(-58.85, -14.03) * mm]});
            skFitSpline(sketch, "E290", {"points": [v(-58.85, -14.03) * mm, v(-64.4, -14.03) * mm, v(-67.2, -10.2) * mm, v(-67.2, -2.55) * mm]});
            skFitSpline(sketch, "E291", {"points": [v(-67.2, -2.55) * mm, v(-67.2, -0.18) * mm, v(-66.96, 1.8) * mm, v(-66.5, 3.4) * mm]});
            skFitSpline(sketch, "E292", {"points": [v(-66.5, 3.4) * mm, v(-66, 5.04) * mm, v(-65.36, 6.35) * mm, v(-64.56, 7.34) * mm]});
            skFitSpline(sketch, "E293", {"points": [v(-64.56, 7.34) * mm, v(-63.76, 8.37) * mm, v(-62.83, 9.1) * mm, v(-61.76, 9.51) * mm]});
            skFitSpline(sketch, "E294", {"points": [v(-61.76, 9.51) * mm, v(-60.66, 9.97) * mm, v(-59.51, 10.2) * mm, v(-58.33, 10.2) * mm]});
            skFitSpline(sketch, "E295", {"points": [v(-58.33, 10.2) * mm, v(-57.34, 10.2) * mm, v(-56.4, 9.95) * mm, v(-55.48, 9.45) * mm]});
            skFitSpline(sketch, "E296", {"points": [v(-55.48, 9.45) * mm, v(-54.52, 9) * mm, v(-53.7, 8.31) * mm, v(-53.02, 7.4) * mm]});
            skFitSpline(sketch, "E297", {"points": [v(-53.02, 7.4) * mm, v(-52.3, 6.48) * mm, v(-51.72, 5.34) * mm, v(-51.3, 3.97) * mm]});
            skFitSpline(sketch, "E298", {"points": [v(-51.3, 3.97) * mm, v(-50.85, 2.64) * mm, v(-50.62, 1.1) * mm, v(-50.62, -0.66) * mm]});
            skFitSpline(sketch, "E299", {"points": [v(-45.6, -0.83) * mm, v(-45.6, 0.96) * mm, v(-45.84, 2.65) * mm, v(-46.33, 4.25) * mm]});
            skFitSpline(sketch, "E300", {"points": [v(-46.33, 4.25) * mm, v(-46.8, 5.9) * mm, v(-47.5, 7.32) * mm, v(-48.45, 8.54) * mm]});
            skFitSpline(sketch, "E301", {"points": [v(-48.45, 8.54) * mm, v(-49.4, 9.76) * mm, v(-50.6, 10.73) * mm, v(-52.05, 11.45) * mm]});
            skFitSpline(sketch, "E302", {"points": [v(-52.05, 11.45) * mm, v(-53.5, 12.22) * mm, v(-55.2, 12.6) * mm, v(-57.2, 12.6) * mm]});
            skFitSpline(sketch, "E303", {"points": [v(-57.2, 12.6) * mm, v(-59.25, 12.6) * mm, v(-61.06, 12.12) * mm, v(-62.62, 11.17) * mm]});
            skFitSpline(sketch, "E304", {"points": [v(-62.62, 11.17) * mm, v(-64.18, 10.22) * mm, v(-65.6, 8.71) * mm, v(-66.9, 6.65) * mm]});
            skFitSpline(sketch, "E305", {"points": [v(-67.02, 6.65) * mm, v(-66.98, 8.4) * mm, v(-66.94, 10.35) * mm, v(-66.9, 12.48) * mm]});
            skFitSpline(sketch, "E306", {"points": [v(-66.9, 12.48) * mm, v(-66.87, 14.65) * mm, v(-66.83, 16.75) * mm, v(-66.8, 18.77) * mm]});
            skFitSpline(sketch, "E307", {"points": [v(-66.8, 18.77) * mm, v(-66.75, 20.83) * mm, v(-66.7, 22.67) * mm, v(-66.62, 24.31) * mm]});
            skFitSpline(sketch, "E308", {"points": [v(-66.62, 24.31) * mm, v(-66.54, 25.99) * mm, v(-66.45, 27.2) * mm, v(-66.33, 27.97) * mm]});
            skFitSpline(sketch, "E309", {"points": [v(-66.33, 27.97) * mm, v(-66.87, 27.9) * mm, v(-67.36, 27.82) * mm, v(-67.82, 27.74) * mm]});
            skFitSpline(sketch, "E310", {"points": [v(-67.82, 27.74) * mm, v(-68.28, 27.7) * mm, v(-68.71, 27.68) * mm, v(-69.13, 27.68) * mm]});
            skFitSpline(sketch, "E311", {"points": [v(-69.13, 27.68) * mm, v(-69.78, 27.68) * mm, v(-70.64, 27.78) * mm, v(-71.7, 27.97) * mm]});
            skFitSpline(sketch, "E312", {"points": [v(-71.7, 27.97) * mm, v(-71.63, 27.02) * mm, v(-71.57, 25.85) * mm, v(-71.53, 24.48) * mm]});
            skFitSpline(sketch, "E313", {"points": [v(-71.53, 24.48) * mm, v(-71.46, 23.15) * mm, v(-71.4, 21.74) * mm, v(-71.36, 20.25) * mm]});
            skFitSpline(sketch, "E314", {"points": [v(-71.36, 20.25) * mm, v(-71.32, 18.77) * mm, v(-71.3, 17.26) * mm, v(-71.3, 15.74) * mm]});
            skFitSpline(sketch, "E315", {"points": [v(-71.3, 15.74) * mm, v(-71.27, 14.22) * mm, v(-71.25, 12.8) * mm, v(-71.25, 11.51) * mm]});
            skLineSegment(sketch, "E316", {"start": v(-66.9, 6.65) * mm, "end": v(-67.02, 6.65) * mm});
            skLineSegment(sketch, "E317", {"start": v(-67.02, 6.65) * mm, "end": v(-66.9, 6.65) * mm});
            skFitSpline(sketch, "E318", {"points": [v(-71.25, 1.17) * mm, v(-71.25, -0.13) * mm, v(-71.27, -1.54) * mm, v(-71.3, -3.06) * mm]});
            skFitSpline(sketch, "E319", {"points": [v(-71.3, -3.06) * mm, v(-71.3, -4.58) * mm, v(-71.32, -6.09) * mm, v(-71.36, -7.57) * mm]});
            skFitSpline(sketch, "E320", {"points": [v(-71.36, -7.57) * mm, v(-71.4, -9.02) * mm, v(-71.46, -10.4) * mm, v(-71.53, -11.69) * mm]});
            skFitSpline(sketch, "E321", {"points": [v(-71.53, -11.69) * mm, v(-71.57, -12.98) * mm, v(-71.63, -14.09) * mm, v(-71.7, -15) * mm]});
            skLineSegment(sketch, "E322", {"start": v(-71.25, 11.51) * mm, "end": v(-71.25, 1.17) * mm});
            skLineSegment(sketch, "E323", {"start": v(-71.25, 1.17) * mm, "end": v(-71.25, 11.51) * mm});
            skFitSpline(sketch, "E324", {"points": [v(-70.68, -15) * mm, v(-69.5, -13.9) * mm, v(-68.22, -12.8) * mm, v(-66.85, -11.69) * mm]});
            skFitSpline(sketch, "E325", {"points": [v(-66.85, -11.69) * mm, v(-66.09, -12.8) * mm, v(-64.98, -13.75) * mm, v(-63.53, -14.55) * mm]});
            skFitSpline(sketch, "E326", {"points": [v(-63.53, -14.55) * mm, v(-62.05, -15.3) * mm, v(-60.4, -15.69) * mm, v(-58.56, -15.69) * mm]});
            skFitSpline(sketch, "E327", {"points": [v(-58.56, -15.69) * mm, v(-56.73, -15.69) * mm, v(-55.04, -15.35) * mm, v(-53.48, -14.66) * mm]});
            skFitSpline(sketch, "E328", {"points": [v(-53.48, -14.66) * mm, v(-51.88, -13.94) * mm, v(-50.5, -12.93) * mm, v(-49.36, -11.63) * mm]});
            skFitSpline(sketch, "E329", {"points": [v(-49.36, -11.63) * mm, v(-48.18, -10.3) * mm, v(-47.27, -8.72) * mm, v(-46.62, -6.89) * mm]});
            skFitSpline(sketch, "E330", {"points": [v(-46.62, -6.89) * mm, v(-45.93, -5.06) * mm, v(-45.6, -3.04) * mm, v(-45.6, -0.83) * mm]});
            skLineSegment(sketch, "E331", {"start": v(-71.7, -15) * mm, "end": v(-70.68, -15) * mm});
            skLineSegment(sketch, "E332", {"start": v(-70.68, -15) * mm, "end": v(-71.7, -15) * mm});
            skFitSpline(sketch, "E333", {"points": [v(-27.95, 10.77) * mm, v(-26.47, 10.77) * mm, v(-25.27, 10.45) * mm, v(-24.35, 9.8) * mm]});
            skFitSpline(sketch, "E334", {"points": [v(-24.35, 9.8) * mm, v(-23.44, 9.15) * mm, v(-22.73, 8.33) * mm, v(-22.24, 7.34) * mm]});
            skFitSpline(sketch, "E335", {"points": [v(-22.24, 7.34) * mm, v(-21.7, 6.35) * mm, v(-21.36, 5.28) * mm, v(-21.21, 4.14) * mm]});
            skFitSpline(sketch, "E336", {"points": [v(-21.21, 4.14) * mm, v(-21.02, 3) * mm, v(-20.93, 1.91) * mm, v(-20.93, 0.88) * mm]});
            skFitSpline(sketch, "E337", {"points": [v(-20.93, 0.88) * mm, v(-22.14, 0.85) * mm, v(-23.4, 0.8) * mm, v(-24.7, 0.77) * mm]});
            skFitSpline(sketch, "E338", {"points": [v(-24.7, 0.77) * mm, v(-26, 0.73) * mm, v(-27.27, 0.71) * mm, v(-28.53, 0.71) * mm]});
            skFitSpline(sketch, "E339", {"points": [v(-28.53, 0.71) * mm, v(-29.74, 0.71) * mm, v(-31, 0.73) * mm, v(-32.3, 0.77) * mm]});
            skFitSpline(sketch, "E340", {"points": [v(-32.3, 0.77) * mm, v(-33.55, 0.8) * mm, v(-34.77, 0.85) * mm, v(-35.95, 0.88) * mm]});
            skFitSpline(sketch, "E341", {"points": [v(-35.95, 0.88) * mm, v(-35.88, 1.91) * mm, v(-35.69, 3) * mm, v(-35.38, 4.14) * mm]});
            skFitSpline(sketch, "E342", {"points": [v(-35.38, 4.14) * mm, v(-35.04, 5.32) * mm, v(-34.56, 6.39) * mm, v(-33.95, 7.34) * mm]});
            skFitSpline(sketch, "E343", {"points": [v(-33.95, 7.34) * mm, v(-33.3, 8.33) * mm, v(-32.5, 9.15) * mm, v(-31.55, 9.8) * mm]});
            skFitSpline(sketch, "E344", {"points": [v(-31.55, 9.8) * mm, v(-30.56, 10.45) * mm, v(-29.36, 10.77) * mm, v(-27.95, 10.77) * mm]});
            skFitSpline(sketch, "E345", {"points": [v(-41.15, -2.43) * mm, v(-41.15, -4.34) * mm, v(-40.83, -6.1) * mm, v(-40.18, -7.75) * mm]});
            skFitSpline(sketch, "E346", {"points": [v(-40.18, -7.75) * mm, v(-39.5, -9.38) * mm, v(-38.54, -10.81) * mm, v(-37.33, -12.03) * mm]});
            skFitSpline(sketch, "E347", {"points": [v(-37.33, -12.03) * mm, v(-36.07, -13.21) * mm, v(-34.6, -14.13) * mm, v(-32.93, -14.77) * mm]});
            skFitSpline(sketch, "E348", {"points": [v(-32.93, -14.77) * mm, v(-31.21, -15.38) * mm, v(-29.33, -15.69) * mm, v(-27.27, -15.69) * mm]});
            skFitSpline(sketch, "E349", {"points": [v(-27.27, -15.69) * mm, v(-25.44, -15.69) * mm, v(-23.69, -15.36) * mm, v(-22.01, -14.72) * mm]});
            skFitSpline(sketch, "E350", {"points": [v(-22.01, -14.72) * mm, v(-20.3, -14.07) * mm, v(-18.87, -13.29) * mm, v(-17.73, -12.37) * mm]});
            skFitSpline(sketch, "E351", {"points": [v(-17.67, -9.4) * mm, v(-18.16, -9.97) * mm, v(-18.75, -10.5) * mm, v(-19.44, -11) * mm]});
            skFitSpline(sketch, "E352", {"points": [v(-19.44, -11) * mm, v(-20.09, -11.5) * mm, v(-20.8, -11.94) * mm, v(-21.55, -12.32) * mm]});
            skFitSpline(sketch, "E353", {"points": [v(-21.55, -12.32) * mm, v(-22.32, -12.66) * mm, v(-23.1, -12.95) * mm, v(-23.9, -13.17) * mm]});
            skFitSpline(sketch, "E354", {"points": [v(-23.9, -13.17) * mm, v(-24.7, -13.36) * mm, v(-25.48, -13.46) * mm, v(-26.24, -13.46) * mm]});
            skFitSpline(sketch, "E355", {"points": [v(-26.24, -13.46) * mm, v(-27.84, -13.46) * mm, v(-29.25, -13.2) * mm, v(-30.47, -12.66) * mm]});
            skFitSpline(sketch, "E356", {"points": [v(-30.47, -12.66) * mm, v(-31.69, -12.09) * mm, v(-32.72, -11.35) * mm, v(-33.55, -10.43) * mm]});
            skFitSpline(sketch, "E357", {"points": [v(-33.55, -10.43) * mm, v(-34.4, -9.48) * mm, v(-35.04, -8.35) * mm, v(-35.5, -7.06) * mm]});
            skFitSpline(sketch, "E358", {"points": [v(-35.5, -7.06) * mm, v(-35.92, -5.76) * mm, v(-36.13, -4.37) * mm, v(-36.13, -2.89) * mm]});
            skLineSegment(sketch, "E359", {"start": v(-17.73, -12.37) * mm, "end": v(-17.38, -9.57) * mm});
            skLineSegment(sketch, "E360", {"start": v(-17.38, -9.57) * mm, "end": v(-17.67, -9.4) * mm});
            skLineSegment(sketch, "E361", {"start": v(-17.67, -9.4) * mm, "end": v(-17.73, -12.37) * mm});
            skFitSpline(sketch, "E362", {"points": [v(-36.13, -2.15) * mm, v(-36.13, -1.76) * mm, v(-36.1, -1.48) * mm, v(-36.07, -1.29) * mm]});
            skFitSpline(sketch, "E363", {"points": [v(-36.07, -1.29) * mm, v(-34.81, -1.25) * mm, v(-33.57, -1.21) * mm, v(-32.35, -1.17) * mm]});
            skFitSpline(sketch, "E364", {"points": [v(-32.35, -1.17) * mm, v(-31.1, -1.14) * mm, v(-29.84, -1.12) * mm, v(-28.58, -1.12) * mm]});
            skFitSpline(sketch, "E365", {"points": [v(-28.58, -1.12) * mm, v(-26.53, -1.12) * mm, v(-24.49, -1.14) * mm, v(-22.47, -1.17) * mm]});
            skFitSpline(sketch, "E366", {"points": [v(-22.47, -1.17) * mm, v(-20.45, -1.21) * mm, v(-18.41, -1.25) * mm, v(-16.35, -1.29) * mm]});
            skFitSpline(sketch, "E367", {"points": [v(-16.35, -1.29) * mm, v(-16.32, -0.9) * mm, v(-16.3, -0.55) * mm, v(-16.3, -0.2) * mm]});
            skFitSpline(sketch, "E368", {"points": [v(-16.3, -0.2) * mm, v(-16.26, 0.18) * mm, v(-16.24, 0.56) * mm, v(-16.24, 0.94) * mm]});
            skFitSpline(sketch, "E369", {"points": [v(-16.24, 0.94) * mm, v(-16.24, 2.54) * mm, v(-16.49, 4.05) * mm, v(-16.98, 5.45) * mm]});
            skFitSpline(sketch, "E370", {"points": [v(-16.98, 5.45) * mm, v(-17.44, 6.86) * mm, v(-18.16, 8.08) * mm, v(-19.15, 9.11) * mm]});
            skFitSpline(sketch, "E371", {"points": [v(-19.15, 9.11) * mm, v(-20.14, 10.18) * mm, v(-21.38, 11.02) * mm, v(-22.87, 11.63) * mm]});
            skFitSpline(sketch, "E372", {"points": [v(-22.87, 11.63) * mm, v(-24.32, 12.27) * mm, v(-26.05, 12.6) * mm, v(-28.07, 12.6) * mm]});
            skFitSpline(sketch, "E373", {"points": [v(-28.07, 12.6) * mm, v(-32.33, 12.6) * mm, v(-35.6, 11.26) * mm, v(-37.84, 8.6) * mm]});
            skFitSpline(sketch, "E374", {"points": [v(-37.84, 8.6) * mm, v(-40.05, 5.93) * mm, v(-41.15, 2.25) * mm, v(-41.15, -2.43) * mm]});
            skLineSegment(sketch, "E375", {"start": v(-36.13, -2.89) * mm, "end": v(-36.13, -2.15) * mm});
            skLineSegment(sketch, "E376", {"start": v(-36.13, -2.15) * mm, "end": v(-36.13, -2.89) * mm});
            skFitSpline(sketch, "E377", {"points": [v(-9.9, 1.17) * mm, v(-9.9, -0.13) * mm, v(-9.91, -1.54) * mm, v(-9.95, -3.06) * mm]});
            skFitSpline(sketch, "E378", {"points": [v(-9.95, -3.06) * mm, v(-9.95, -4.58) * mm, v(-9.97, -6.09) * mm, v(-10, -7.57) * mm]});
            skFitSpline(sketch, "E379", {"points": [v(-10, -7.57) * mm, v(-10.05, -9.06) * mm, v(-10.1, -10.47) * mm, v(-10.18, -11.8) * mm]});
            skFitSpline(sketch, "E380", {"points": [v(-10.18, -11.8) * mm, v(-10.22, -13.14) * mm, v(-10.28, -14.24) * mm, v(-10.35, -15.12) * mm]});
            skFitSpline(sketch, "E381", {"points": [v(-10.35, -15.12) * mm, v(-9.48, -15.04) * mm, v(-8.62, -15) * mm, v(-7.78, -15) * mm]});
            skFitSpline(sketch, "E382", {"points": [v(-7.78, -15) * mm, v(-6.94, -15) * mm, v(-6.08, -15.04) * mm, v(-5.2, -15.12) * mm]});
            skFitSpline(sketch, "E383", {"points": [v(-5.2, -15.12) * mm, v(-5.28, -14.28) * mm, v(-5.36, -13.2) * mm, v(-5.44, -11.86) * mm]});
            skFitSpline(sketch, "E384", {"points": [v(-5.44, -11.86) * mm, v(-5.48, -10.53) * mm, v(-5.51, -9.15) * mm, v(-5.55, -7.75) * mm]});
            skFitSpline(sketch, "E385", {"points": [v(-5.55, -7.75) * mm, v(-5.59, -6.3) * mm, v(-5.63, -4.87) * mm, v(-5.67, -3.46) * mm]});
            skFitSpline(sketch, "E386", {"points": [v(-5.67, -3.46) * mm, v(-5.67, -2.05) * mm, v(-5.67, -0.81) * mm, v(-5.67, 0.25) * mm]});
            skFitSpline(sketch, "E387", {"points": [v(-5.67, 0.25) * mm, v(-5.67, 3.23) * mm, v(-5.06, 5.53) * mm, v(-3.84, 7.17) * mm]});
            skFitSpline(sketch, "E388", {"points": [v(-3.84, 7.17) * mm, v(-2.58, 8.8) * mm, v(-0.62, 9.63) * mm, v(2.05, 9.63) * mm]});
            skFitSpline(sketch, "E389", {"points": [v(2.05, 9.63) * mm, v(4, 9.63) * mm, v(5.52, 8.88) * mm, v(6.62, 7.4) * mm]});
            skFitSpline(sketch, "E390", {"points": [v(6.62, 7.4) * mm, v(7.72, 5.95) * mm, v(8.28, 3.8) * mm, v(8.28, 0.94) * mm]});
            skLineSegment(sketch, "E391", {"start": v(-9.9, 11.51) * mm, "end": v(-9.9, 1.17) * mm});
            skLineSegment(sketch, "E392", {"start": v(-9.9, 1.17) * mm, "end": v(-9.9, 11.51) * mm});
            skFitSpline(sketch, "E393", {"points": [v(8.28, -2.55) * mm, v(8.28, -4.75) * mm, v(8.22, -6.9) * mm, v(8.1, -9) * mm]});
            skFitSpline(sketch, "E394", {"points": [v(8.1, -9) * mm, v(8.03, -11.1) * mm, v(7.95, -13.14) * mm, v(7.88, -15.12) * mm]});
            skFitSpline(sketch, "E395", {"points": [v(7.88, -15.12) * mm, v(8.64, -15.04) * mm, v(9.42, -15) * mm, v(10.22, -15) * mm]});
            skFitSpline(sketch, "E396", {"points": [v(10.22, -15) * mm, v(11.06, -15) * mm, v(11.86, -15.04) * mm, v(12.62, -15.12) * mm]});
            skFitSpline(sketch, "E397", {"points": [v(12.62, -15.12) * mm, v(12.58, -14.58) * mm, v(12.54, -14.03) * mm, v(12.5, -13.46) * mm]});
            skFitSpline(sketch, "E398", {"points": [v(12.5, -13.46) * mm, v(12.5, -12.85) * mm, v(12.5, -12.24) * mm, v(12.5, -11.63) * mm]});
            skLineSegment(sketch, "E399", {"start": v(8.28, 0.94) * mm, "end": v(8.28, -2.55) * mm});
            skLineSegment(sketch, "E400", {"start": v(8.28, -2.55) * mm, "end": v(8.28, 0.94) * mm});
            skFitSpline(sketch, "E401", {"points": [v(12.5, -7.92) * mm, v(12.5, -5.97) * mm, v(12.54, -4.15) * mm, v(12.62, -2.43) * mm]});
            skFitSpline(sketch, "E402", {"points": [v(12.62, -2.43) * mm, v(12.7, -0.68) * mm, v(12.73, 1.02) * mm, v(12.73, 2.65) * mm]});
            skFitSpline(sketch, "E403", {"points": [v(12.73, 2.65) * mm, v(12.73, 4.64) * mm, v(12.45, 6.25) * mm, v(11.88, 7.51) * mm]});
            skFitSpline(sketch, "E404", {"points": [v(11.88, 7.51) * mm, v(11.34, 8.8) * mm, v(10.64, 9.82) * mm, v(9.76, 10.54) * mm]});
            skFitSpline(sketch, "E405", {"points": [v(9.76, 10.54) * mm, v(8.89, 11.3) * mm, v(7.9, 11.84) * mm, v(6.8, 12.14) * mm]});
            skFitSpline(sketch, "E406", {"points": [v(6.8, 12.14) * mm, v(5.72, 12.45) * mm, v(4.66, 12.6) * mm, v(3.6, 12.6) * mm]});
            skFitSpline(sketch, "E407", {"points": [v(3.6, 12.6) * mm, v(1.53, 12.6) * mm, v(-0.24, 12.14) * mm, v(-1.72, 11.23) * mm]});
            skFitSpline(sketch, "E408", {"points": [v(-1.72, 11.23) * mm, v(-3.2, 10.35) * mm, v(-4.48, 9.1) * mm, v(-5.55, 7.45) * mm]});
            skLineSegment(sketch, "E409", {"start": v(12.5, -11.63) * mm, "end": v(12.5, -7.92) * mm});
            skLineSegment(sketch, "E410", {"start": v(12.5, -7.92) * mm, "end": v(12.5, -11.63) * mm});
            skFitSpline(sketch, "E411", {"points": [v(-5.67, 11.8) * mm, v(-5.67, 13.05) * mm, v(-5.67, 14.43) * mm, v(-5.67, 15.91) * mm]});
            skFitSpline(sketch, "E412", {"points": [v(-5.67, 15.91) * mm, v(-5.63, 17.4) * mm, v(-5.59, 18.86) * mm, v(-5.55, 20.31) * mm]});
            skFitSpline(sketch, "E413", {"points": [v(-5.55, 20.31) * mm, v(-5.51, 21.8) * mm, v(-5.48, 23.2) * mm, v(-5.44, 24.54) * mm]});
            skFitSpline(sketch, "E414", {"points": [v(-5.44, 24.54) * mm, v(-5.36, 25.87) * mm, v(-5.28, 27.02) * mm, v(-5.2, 27.97) * mm]});
            skFitSpline(sketch, "E415", {"points": [v(-5.2, 27.97) * mm, v(-6.28, 27.78) * mm, v(-7.13, 27.68) * mm, v(-7.78, 27.68) * mm]});
            skFitSpline(sketch, "E416", {"points": [v(-7.78, 27.68) * mm, v(-8.43, 27.68) * mm, v(-9.28, 27.78) * mm, v(-10.35, 27.97) * mm]});
            skFitSpline(sketch, "E417", {"points": [v(-10.35, 27.97) * mm, v(-10.28, 27.02) * mm, v(-10.22, 25.85) * mm, v(-10.18, 24.48) * mm]});
            skFitSpline(sketch, "E418", {"points": [v(-10.18, 24.48) * mm, v(-10.1, 23.15) * mm, v(-10.05, 21.74) * mm, v(-10, 20.25) * mm]});
            skFitSpline(sketch, "E419", {"points": [v(-10, 20.25) * mm, v(-9.97, 18.77) * mm, v(-9.95, 17.26) * mm, v(-9.95, 15.74) * mm]});
            skFitSpline(sketch, "E420", {"points": [v(-9.95, 15.74) * mm, v(-9.91, 14.22) * mm, v(-9.9, 12.8) * mm, v(-9.9, 11.51) * mm]});
            skLineSegment(sketch, "E421", {"start": v(-5.55, 7.45) * mm, "end": v(-5.67, 7.45) * mm});
            skLineSegment(sketch, "E422", {"start": v(-5.67, 7.45) * mm, "end": v(-5.67, 11.8) * mm});
            skLineSegment(sketch, "E423", {"start": v(-5.67, 11.8) * mm, "end": v(-5.55, 7.45) * mm});
            skFitSpline(sketch, "E424", {"points": [v(35.8, -9.46) * mm, v(35.15, -10.53) * mm, v(34.22, -11.46) * mm, v(33, -12.26) * mm]});
            skFitSpline(sketch, "E425", {"points": [v(33, -12.26) * mm, v(31.82, -13.06) * mm, v(30.5, -13.46) * mm, v(29.06, -13.46) * mm]});
            skFitSpline(sketch, "E426", {"points": [v(29.06, -13.46) * mm, v(27.8, -13.46) * mm, v(26.66, -13) * mm, v(25.63, -12.09) * mm]});
            skFitSpline(sketch, "E427", {"points": [v(25.63, -12.09) * mm, v(24.6, -11.17) * mm, v(24.09, -9.82) * mm, v(24.09, -8.03) * mm]});
            skFitSpline(sketch, "E428", {"points": [v(24.09, -8.03) * mm, v(24.09, -6.96) * mm, v(24.28, -6.09) * mm, v(24.66, -5.4) * mm]});
            skFitSpline(sketch, "E429", {"points": [v(24.66, -5.4) * mm, v(25.08, -4.72) * mm, v(25.61, -4.15) * mm, v(26.26, -3.69) * mm]});
            skFitSpline(sketch, "E430", {"points": [v(26.26, -3.69) * mm, v(26.95, -3.23) * mm, v(27.7, -2.87) * mm, v(28.55, -2.6) * mm]});
            skFitSpline(sketch, "E431", {"points": [v(28.55, -2.6) * mm, v(29.42, -2.34) * mm, v(30.3, -2.13) * mm, v(31.17, -1.97) * mm]});
            skFitSpline(sketch, "E432", {"points": [v(31.17, -1.97) * mm, v(32.05, -1.78) * mm, v(32.9, -1.61) * mm, v(33.75, -1.46) * mm]});
            skFitSpline(sketch, "E433", {"points": [v(33.75, -1.46) * mm, v(34.62, -1.3) * mm, v(35.38, -1.12) * mm, v(36.03, -0.89) * mm]});
            skLineSegment(sketch, "E434", {"start": v(36.03, -0.89) * mm, "end": v(35.8, -9.46) * mm});
            skLineSegment(sketch, "E435", {"start": v(35.8, -9.46) * mm, "end": v(36.03, -0.89) * mm});
            skFitSpline(sketch, "E436", {"points": [v(22.55, 6.31) * mm, v(23.2, 7.53) * mm, v(24.16, 8.48) * mm, v(25.46, 9.17) * mm]});
            skFitSpline(sketch, "E437", {"points": [v(25.46, 9.17) * mm, v(26.8, 9.85) * mm, v(28.22, 10.2) * mm, v(29.75, 10.2) * mm]});
            skFitSpline(sketch, "E438", {"points": [v(29.75, 10.2) * mm, v(30.89, 10.2) * mm, v(31.86, 9.99) * mm, v(32.66, 9.57) * mm]});
            skFitSpline(sketch, "E439", {"points": [v(32.66, 9.57) * mm, v(33.46, 9.19) * mm, v(34.1, 8.67) * mm, v(34.6, 8.03) * mm]});
            skFitSpline(sketch, "E440", {"points": [v(34.6, 8.03) * mm, v(35.1, 7.38) * mm, v(35.46, 6.62) * mm, v(35.69, 5.74) * mm]});
            skFitSpline(sketch, "E441", {"points": [v(35.69, 5.74) * mm, v(35.92, 4.86) * mm, v(36.03, 3.95) * mm, v(36.03, 3) * mm]});
            skFitSpline(sketch, "E442", {"points": [v(36.03, 3) * mm, v(36.03, 2.43) * mm, v(35.97, 1.95) * mm, v(35.86, 1.57) * mm]});
            skFitSpline(sketch, "E443", {"points": [v(35.86, 1.57) * mm, v(35.75, 1.23) * mm, v(35.4, 0.92) * mm, v(34.83, 0.65) * mm]});
            skFitSpline(sketch, "E444", {"points": [v(34.83, 0.65) * mm, v(34.3, 0.39) * mm, v(33.44, 0.12) * mm, v(32.26, -0.15) * mm]});
            skFitSpline(sketch, "E445", {"points": [v(32.26, -0.15) * mm, v(31.12, -0.37) * mm, v(29.52, -0.66) * mm, v(27.46, -1) * mm]});
            skFitSpline(sketch, "E446", {"points": [v(27.46, -1) * mm, v(24.95, -1.42) * mm, v(22.96, -2.26) * mm, v(21.52, -3.52) * mm]});
            skFitSpline(sketch, "E447", {"points": [v(21.52, -3.52) * mm, v(20.1, -4.77) * mm, v(19.4, -6.55) * mm, v(19.4, -8.83) * mm]});
            skFitSpline(sketch, "E448", {"points": [v(19.4, -8.83) * mm, v(19.4, -9.94) * mm, v(19.61, -10.93) * mm, v(20.03, -11.8) * mm]});
            skFitSpline(sketch, "E449", {"points": [v(20.03, -11.8) * mm, v(20.49, -12.64) * mm, v(21.06, -13.36) * mm, v(21.75, -13.97) * mm]});
            skFitSpline(sketch, "E450", {"points": [v(21.75, -13.97) * mm, v(22.47, -14.58) * mm, v(23.29, -15.02) * mm, v(24.2, -15.29) * mm]});
            skFitSpline(sketch, "E451", {"points": [v(24.2, -15.29) * mm, v(25.12, -15.55) * mm, v(26.05, -15.69) * mm, v(27, -15.69) * mm]});
            skFitSpline(sketch, "E452", {"points": [v(27, -15.69) * mm, v(28.95, -15.69) * mm, v(30.58, -15.36) * mm, v(31.92, -14.72) * mm]});
            skFitSpline(sketch, "E453", {"points": [v(31.92, -14.72) * mm, v(33.25, -14.07) * mm, v(34.6, -13.06) * mm, v(35.97, -11.69) * mm]});
            skFitSpline(sketch, "E454", {"points": [v(35.97, -11.69) * mm, v(36.09, -12.68) * mm, v(36.47, -13.5) * mm, v(37.12, -14.15) * mm]});
            skFitSpline(sketch, "E455", {"points": [v(37.12, -14.15) * mm, v(37.76, -14.75) * mm, v(38.7, -15.06) * mm, v(39.92, -15.06) * mm]});
            skFitSpline(sketch, "E456", {"points": [v(39.92, -15.06) * mm, v(40.68, -15.06) * mm, v(41.36, -15) * mm, v(41.97, -14.89) * mm]});
            skFitSpline(sketch, "E457", {"points": [v(41.97, -14.89) * mm, v(42.62, -14.77) * mm, v(43.15, -14.62) * mm, v(43.57, -14.43) * mm]});
            skLineSegment(sketch, "E458", {"start": v(21.92, 9.28) * mm, "end": v(21.92, 6.31) * mm});
            skLineSegment(sketch, "E459", {"start": v(21.92, 6.31) * mm, "end": v(22.55, 6.31) * mm});
            skLineSegment(sketch, "E460", {"start": v(22.55, 6.31) * mm, "end": v(21.92, 9.28) * mm});
            skFitSpline(sketch, "E461", {"points": [v(43.57, -13.17) * mm, v(43.38, -13.29) * mm, v(43.17, -13.36) * mm, v(42.95, -13.4) * mm]});
            skFitSpline(sketch, "E462", {"points": [v(42.95, -13.4) * mm, v(42.75, -13.4) * mm, v(42.56, -13.4) * mm, v(42.37, -13.4) * mm]});
            skFitSpline(sketch, "E463", {"points": [v(42.37, -13.4) * mm, v(41.8, -13.4) * mm, v(41.36, -13.27) * mm, v(41.06, -13) * mm]});
            skFitSpline(sketch, "E464", {"points": [v(41.06, -13) * mm, v(40.8, -12.74) * mm, v(40.58, -12.41) * mm, v(40.43, -12.03) * mm]});
            skFitSpline(sketch, "E465", {"points": [v(40.43, -12.03) * mm, v(40.28, -11.61) * mm, v(40.18, -11.15) * mm, v(40.15, -10.66) * mm]});
            skFitSpline(sketch, "E466", {"points": [v(40.15, -10.66) * mm, v(40.15, -10.13) * mm, v(40.15, -9.63) * mm, v(40.15, -9.17) * mm]});
            skFitSpline(sketch, "E467", {"points": [v(40.15, -9.17) * mm, v(40.15, -6.77) * mm, v(40.18, -4.5) * mm, v(40.26, -2.37) * mm]});
            skFitSpline(sketch, "E468", {"points": [v(40.26, -2.37) * mm, v(40.34, -0.2) * mm, v(40.37, 1.97) * mm, v(40.37, 4.14) * mm]});
            skFitSpline(sketch, "E469", {"points": [v(40.37, 4.14) * mm, v(40.37, 5.4) * mm, v(40.15, 6.54) * mm, v(39.69, 7.57) * mm]});
            skFitSpline(sketch, "E470", {"points": [v(39.69, 7.57) * mm, v(39.23, 8.64) * mm, v(38.6, 9.53) * mm, v(37.8, 10.25) * mm]});
            skFitSpline(sketch, "E471", {"points": [v(37.8, 10.25) * mm, v(37, 11.02) * mm, v(36.03, 11.59) * mm, v(34.89, 11.97) * mm]});
            skFitSpline(sketch, "E472", {"points": [v(34.89, 11.97) * mm, v(33.75, 12.39) * mm, v(32.49, 12.6) * mm, v(31.12, 12.6) * mm]});
            skFitSpline(sketch, "E473", {"points": [v(31.12, 12.6) * mm, v(29.6, 12.6) * mm, v(28.1, 12.37) * mm, v(26.66, 11.91) * mm]});
            skFitSpline(sketch, "E474", {"points": [v(26.66, 11.91) * mm, v(25.21, 11.45) * mm, v(23.63, 10.58) * mm, v(21.92, 9.28) * mm]});
            skLineSegment(sketch, "E475", {"start": v(43.57, -14.43) * mm, "end": v(43.57, -13.17) * mm});
            skLineSegment(sketch, "E476", {"start": v(43.57, -13.17) * mm, "end": v(43.57, -14.43) * mm});
            skFitSpline(sketch, "E477", {"points": [v(68.43, -2.55) * mm, v(68.43, -4.75) * mm, v(68.38, -6.9) * mm, v(68.26, -9) * mm]});
            skFitSpline(sketch, "E478", {"points": [v(68.26, -9) * mm, v(68.19, -11.1) * mm, v(68.1, -13.14) * mm, v(68.03, -15.12) * mm]});
            skFitSpline(sketch, "E479", {"points": [v(68.03, -15.12) * mm, v(68.8, -15.04) * mm, v(69.58, -15) * mm, v(70.38, -15) * mm]});
            skFitSpline(sketch, "E480", {"points": [v(70.38, -15) * mm, v(71.21, -15) * mm, v(72.01, -15.04) * mm, v(72.78, -15.12) * mm]});
            skFitSpline(sketch, "E481", {"points": [v(72.78, -15.12) * mm, v(72.74, -14.58) * mm, v(72.7, -14.03) * mm, v(72.66, -13.46) * mm]});
            skFitSpline(sketch, "E482", {"points": [v(72.66, -13.46) * mm, v(72.66, -12.85) * mm, v(72.66, -12.24) * mm, v(72.66, -11.63) * mm]});
            skLineSegment(sketch, "E483", {"start": v(68.43, 0.94) * mm, "end": v(68.43, -2.55) * mm});
            skLineSegment(sketch, "E484", {"start": v(68.43, -2.55) * mm, "end": v(68.43, 0.94) * mm});
            skFitSpline(sketch, "E485", {"points": [v(72.66, -7.92) * mm, v(72.66, -5.97) * mm, v(72.7, -4.15) * mm, v(72.78, -2.43) * mm]});
            skFitSpline(sketch, "E486", {"points": [v(72.78, -2.43) * mm, v(72.85, -0.68) * mm, v(72.9, 1.02) * mm, v(72.9, 2.65) * mm]});
            skFitSpline(sketch, "E487", {"points": [v(72.9, 2.65) * mm, v(72.9, 4.64) * mm, v(72.6, 6.25) * mm, v(72.03, 7.51) * mm]});
            skFitSpline(sketch, "E488", {"points": [v(72.03, 7.51) * mm, v(71.5, 8.8) * mm, v(70.8, 9.82) * mm, v(69.92, 10.54) * mm]});
            skFitSpline(sketch, "E489", {"points": [v(69.92, 10.54) * mm, v(69.04, 11.3) * mm, v(68.05, 11.84) * mm, v(66.95, 12.14) * mm]});
            skFitSpline(sketch, "E490", {"points": [v(66.95, 12.14) * mm, v(65.88, 12.45) * mm, v(64.81, 12.6) * mm, v(63.75, 12.6) * mm]});
            skFitSpline(sketch, "E491", {"points": [v(63.75, 12.6) * mm, v(61.7, 12.6) * mm, v(59.92, 12.14) * mm, v(58.43, 11.23) * mm]});
            skFitSpline(sketch, "E492", {"points": [v(58.43, 11.23) * mm, v(56.95, 10.35) * mm, v(55.67, 9.1) * mm, v(54.6, 7.45) * mm]});
            skLineSegment(sketch, "E493", {"start": v(72.66, -11.63) * mm, "end": v(72.66, -7.92) * mm});
            skLineSegment(sketch, "E494", {"start": v(72.66, -7.92) * mm, "end": v(72.66, -11.63) * mm});
            skFitSpline(sketch, "E495", {"points": [v(54.5, 7.45) * mm, v(54.5, 8.98) * mm, v(54.55, 10.5) * mm, v(54.66, 12.03) * mm]});
            skFitSpline(sketch, "E496", {"points": [v(54.66, 12.03) * mm, v(54.17, 11.95) * mm, v(53.73, 11.87) * mm, v(53.35, 11.8) * mm]});
            skFitSpline(sketch, "E497", {"points": [v(53.35, 11.8) * mm, v(53, 11.76) * mm, v(52.68, 11.74) * mm, v(52.38, 11.74) * mm]});
            skFitSpline(sketch, "E498", {"points": [v(52.38, 11.74) * mm, v(51.73, 11.74) * mm, v(50.87, 11.84) * mm, v(49.8, 12.03) * mm]});
            skFitSpline(sketch, "E499", {"points": [v(49.8, 12.03) * mm, v(50, 10.39) * mm, v(50.1, 8.62) * mm, v(50.15, 6.71) * mm]});
            skFitSpline(sketch, "E500", {"points": [v(50.15, 6.71) * mm, v(50.22, 4.85) * mm, v(50.26, 3.05) * mm, v(50.26, 1.34) * mm]});
            skLineSegment(sketch, "E501", {"start": v(54.6, 7.45) * mm, "end": v(54.5, 7.45) * mm});
            skLineSegment(sketch, "E502", {"start": v(54.5, 7.45) * mm, "end": v(54.6, 7.45) * mm});
            skFitSpline(sketch, "E503", {"points": [v(50.26, -4.6) * mm, v(50.26, -6.32) * mm, v(50.22, -8.13) * mm, v(50.15, -10.03) * mm]});
            skFitSpline(sketch, "E504", {"points": [v(50.15, -10.03) * mm, v(50.1, -11.9) * mm, v(50, -13.6) * mm, v(49.8, -15.12) * mm]});
            skFitSpline(sketch, "E505", {"points": [v(49.8, -15.12) * mm, v(50.68, -15.04) * mm, v(51.54, -15) * mm, v(52.38, -15) * mm]});
            skFitSpline(sketch, "E506", {"points": [v(52.38, -15) * mm, v(53.21, -15) * mm, v(54.07, -15.04) * mm, v(54.95, -15.12) * mm]});
            skFitSpline(sketch, "E507", {"points": [v(54.95, -15.12) * mm, v(54.76, -13.6) * mm, v(54.62, -11.9) * mm, v(54.55, -10.03) * mm]});
            skFitSpline(sketch, "E508", {"points": [v(54.55, -10.03) * mm, v(54.5, -8.13) * mm, v(54.5, -6.32) * mm, v(54.5, -4.6) * mm]});
            skLineSegment(sketch, "E509", {"start": v(50.26, 1.34) * mm, "end": v(50.26, -4.6) * mm});
            skLineSegment(sketch, "E510", {"start": v(50.26, -4.6) * mm, "end": v(50.26, 1.34) * mm});
            skFitSpline(sketch, "E511", {"points": [v(54.5, 0.25) * mm, v(54.5, 3.23) * mm, v(55.1, 5.53) * mm, v(56.32, 7.17) * mm]});
            skFitSpline(sketch, "E512", {"points": [v(56.32, 7.17) * mm, v(57.58, 8.8) * mm, v(59.54, 9.63) * mm, v(62.2, 9.63) * mm]});
            skFitSpline(sketch, "E513", {"points": [v(62.2, 9.63) * mm, v(64.15, 9.63) * mm, v(65.67, 8.88) * mm, v(66.78, 7.4) * mm]});
            skFitSpline(sketch, "E514", {"points": [v(66.78, 7.4) * mm, v(67.88, 5.95) * mm, v(68.43, 3.8) * mm, v(68.43, 0.94) * mm]});
            skLineSegment(sketch, "E515", {"start": v(54.5, -4.6) * mm, "end": v(54.5, 0.25) * mm});
            skLineSegment(sketch, "E516", {"start": v(54.5, 0.25) * mm, "end": v(54.5, -4.6) * mm});
            skFitSpline(sketch, "E517", {"points": [v(-39.9, -57.3) * mm, v(-39.9, -55.6) * mm, v(-39.74, -54) * mm, v(-39.43, -52.5) * mm]});
            skFitSpline(sketch, "E518", {"points": [v(-39.43, -52.5) * mm, v(-39.1, -50.98) * mm, v(-38.6, -49.67) * mm, v(-37.95, -48.56) * mm]});
            skFitSpline(sketch, "E519", {"points": [v(-37.95, -48.56) * mm, v(-37.26, -47.42) * mm, v(-36.42, -46.55) * mm, v(-35.43, -45.94) * mm]});
            skFitSpline(sketch, "E520", {"points": [v(-35.43, -45.94) * mm, v(-34.4, -45.29) * mm, v(-33.2, -44.96) * mm, v(-31.83, -44.96) * mm]});
            skFitSpline(sketch, "E521", {"points": [v(-31.83, -44.96) * mm, v(-29.1, -44.96) * mm, v(-27.01, -45.94) * mm, v(-25.6, -47.88) * mm]});
            skFitSpline(sketch, "E522", {"points": [v(-25.6, -47.88) * mm, v(-24.2, -49.78) * mm, v(-23.5, -52.56) * mm, v(-23.5, -56.22) * mm]});
            skFitSpline(sketch, "E523", {"points": [v(-23.5, -56.22) * mm, v(-23.5, -57.75) * mm, v(-23.66, -59.27) * mm, v(-24, -60.8) * mm]});
            skFitSpline(sketch, "E524", {"points": [v(-24, -60.8) * mm, v(-24.3, -62.32) * mm, v(-24.82, -63.69) * mm, v(-25.55, -64.9) * mm]});
            skFitSpline(sketch, "E525", {"points": [v(-25.55, -64.9) * mm, v(-26.23, -66.09) * mm, v(-27.1, -67.06) * mm, v(-28.18, -67.82) * mm]});
            skFitSpline(sketch, "E526", {"points": [v(-28.18, -67.82) * mm, v(-29.24, -68.55) * mm, v(-30.52, -68.9) * mm, v(-32, -68.9) * mm]});
            skFitSpline(sketch, "E527", {"points": [v(-32, -68.9) * mm, v(-32.92, -68.9) * mm, v(-33.85, -68.74) * mm, v(-34.8, -68.4) * mm]});
            skFitSpline(sketch, "E528", {"points": [v(-34.8, -68.4) * mm, v(-35.76, -68.05) * mm, v(-36.61, -67.44) * mm, v(-37.38, -66.56) * mm]});
            skFitSpline(sketch, "E529", {"points": [v(-37.38, -66.56) * mm, v(-38.1, -65.65) * mm, v(-38.7, -64.45) * mm, v(-39.2, -62.96) * mm]});
            skFitSpline(sketch, "E530", {"points": [v(-39.2, -62.96) * mm, v(-39.66, -61.48) * mm, v(-39.9, -59.6) * mm, v(-39.9, -57.3) * mm]});
            skFitSpline(sketch, "E531", {"points": [v(-23.72, -70.28) * mm, v(-22.96, -70.2) * mm, v(-22.23, -70.16) * mm, v(-21.55, -70.16) * mm]});
            skFitSpline(sketch, "E532", {"points": [v(-21.55, -70.16) * mm, v(-20.82, -70.16) * mm, v(-20.08, -70.2) * mm, v(-19.32, -70.28) * mm]});
            skFitSpline(sketch, "E533", {"points": [v(-19.32, -70.28) * mm, v(-19.36, -68.07) * mm, v(-19.4, -65.92) * mm, v(-19.43, -63.82) * mm]});
            skFitSpline(sketch, "E534", {"points": [v(-19.43, -63.82) * mm, v(-19.47, -61.73) * mm, v(-19.5, -59.36) * mm, v(-19.5, -56.74) * mm]});
            skFitSpline(sketch, "E535", {"points": [v(-19.5, -56.74) * mm, v(-19.5, -54.3) * mm, v(-19.47, -51.61) * mm, v(-19.43, -48.68) * mm]});
            skFitSpline(sketch, "E536", {"points": [v(-19.43, -48.68) * mm, v(-19.4, -45.75) * mm, v(-19.36, -42.89) * mm, v(-19.32, -40.1) * mm]});
            skFitSpline(sketch, "E537", {"points": [v(-19.32, -40.1) * mm, v(-19.24, -37.33) * mm, v(-19.17, -34.8) * mm, v(-19.1, -32.5) * mm]});
            skFitSpline(sketch, "E538", {"points": [v(-19.1, -32.5) * mm, v(-19.01, -30.18) * mm, v(-18.92, -28.41) * mm, v(-18.8, -27.2) * mm]});
            skFitSpline(sketch, "E539", {"points": [v(-18.8, -27.2) * mm, v(-19.3, -27.27) * mm, v(-19.76, -27.35) * mm, v(-20.18, -27.42) * mm]});
            skFitSpline(sketch, "E540", {"points": [v(-20.18, -27.42) * mm, v(-20.56, -27.46) * mm, v(-20.96, -27.48) * mm, v(-21.38, -27.48) * mm]});
            skFitSpline(sketch, "E541", {"points": [v(-21.38, -27.48) * mm, v(-21.8, -27.48) * mm, v(-22.21, -27.46) * mm, v(-22.63, -27.42) * mm]});
            skFitSpline(sketch, "E542", {"points": [v(-22.63, -27.42) * mm, v(-23.05, -27.35) * mm, v(-23.5, -27.27) * mm, v(-23.95, -27.2) * mm]});
            skFitSpline(sketch, "E543", {"points": [v(-23.95, -27.2) * mm, v(-23.9, -28.1) * mm, v(-23.9, -29.15) * mm, v(-23.9, -30.34) * mm]});
            skFitSpline(sketch, "E544", {"points": [v(-23.9, -30.34) * mm, v(-23.85, -31.52) * mm, v(-23.83, -32.77) * mm, v(-23.83, -34.1) * mm]});
            skFitSpline(sketch, "E545", {"points": [v(-23.83, -34.1) * mm, v(-23.8, -35.44) * mm, v(-23.78, -36.85) * mm, v(-23.78, -38.34) * mm]});
            skFitSpline(sketch, "E546", {"points": [v(-23.78, -38.34) * mm, v(-23.74, -39.78) * mm, v(-23.72, -41.23) * mm, v(-23.72, -42.68) * mm]});
            skLineSegment(sketch, "E547", {"start": v(-23.55, -64.85) * mm, "end": v(-23.72, -70.28) * mm});
            skLineSegment(sketch, "E548", {"start": v(-23.72, -70.28) * mm, "end": v(-23.55, -64.85) * mm});
            skFitSpline(sketch, "E549", {"points": [v(-23.83, -48.28) * mm, v(-25.47, -44.47) * mm, v(-28.4, -42.56) * mm, v(-32.63, -42.56) * mm]});
            skFitSpline(sketch, "E550", {"points": [v(-32.63, -42.56) * mm, v(-34.12, -42.56) * mm, v(-35.6, -42.87) * mm, v(-37.1, -43.48) * mm]});
            skFitSpline(sketch, "E551", {"points": [v(-37.1, -43.48) * mm, v(-38.54, -44.05) * mm, v(-39.85, -44.95) * mm, v(-41.03, -46.16) * mm]});
            skFitSpline(sketch, "E552", {"points": [v(-41.03, -46.16) * mm, v(-42.18, -47.35) * mm, v(-43.1, -48.83) * mm, v(-43.83, -50.62) * mm]});
            skFitSpline(sketch, "E553", {"points": [v(-43.83, -50.62) * mm, v(-44.56, -52.41) * mm, v(-44.92, -54.53) * mm, v(-44.92, -56.96) * mm]});
            skFitSpline(sketch, "E554", {"points": [v(-44.92, -56.96) * mm, v(-44.92, -59.44) * mm, v(-44.6, -61.57) * mm, v(-43.95, -63.36) * mm]});
            skFitSpline(sketch, "E555", {"points": [v(-43.95, -63.36) * mm, v(-43.26, -65.12) * mm, v(-42.39, -66.56) * mm, v(-41.32, -67.7) * mm]});
            skFitSpline(sketch, "E556", {"points": [v(-41.32, -67.7) * mm, v(-40.21, -68.81) * mm, v(-38.98, -69.61) * mm, v(-37.6, -70.1) * mm]});
            skFitSpline(sketch, "E557", {"points": [v(-37.6, -70.1) * mm, v(-36.2, -70.6) * mm, v(-34.77, -70.85) * mm, v(-33.32, -70.85) * mm]});
            skFitSpline(sketch, "E558", {"points": [v(-33.32, -70.85) * mm, v(-31.9, -70.85) * mm, v(-30.67, -70.66) * mm, v(-29.6, -70.28) * mm]});
            skFitSpline(sketch, "E559", {"points": [v(-29.6, -70.28) * mm, v(-28.54, -69.9) * mm, v(-27.62, -69.4) * mm, v(-26.86, -68.8) * mm]});
            skFitSpline(sketch, "E560", {"points": [v(-26.86, -68.8) * mm, v(-26.06, -68.18) * mm, v(-25.41, -67.54) * mm, v(-24.92, -66.85) * mm]});
            skFitSpline(sketch, "E561", {"points": [v(-24.92, -66.85) * mm, v(-24.39, -66.13) * mm, v(-23.97, -65.46) * mm, v(-23.66, -64.85) * mm]});
            skLineSegment(sketch, "E562", {"start": v(-23.72, -42.68) * mm, "end": v(-23.72, -48.28) * mm});
            skLineSegment(sketch, "E563", {"start": v(-23.72, -48.28) * mm, "end": v(-23.83, -48.28) * mm});
            skLineSegment(sketch, "E564", {"start": v(-23.83, -48.28) * mm, "end": v(-23.72, -42.68) * mm});
            skLineSegment(sketch, "E565", {"start": v(-23.66, -64.85) * mm, "end": v(-23.55, -64.85) * mm});
            skLineSegment(sketch, "E566", {"start": v(-23.55, -64.85) * mm, "end": v(-23.66, -64.85) * mm});
            skFitSpline(sketch, "E567", {"points": [v(-9.8, -54) * mm, v(-9.8, -55.29) * mm, v(-9.81, -56.7) * mm, v(-9.85, -58.22) * mm]});
            skFitSpline(sketch, "E568", {"points": [v(-9.85, -58.22) * mm, v(-9.85, -59.75) * mm, v(-9.87, -61.25) * mm, v(-9.9, -62.74) * mm]});
            skFitSpline(sketch, "E569", {"points": [v(-9.9, -62.74) * mm, v(-9.95, -64.22) * mm, v(-10, -65.63) * mm, v(-10.08, -66.96) * mm]});
            skFitSpline(sketch, "E570", {"points": [v(-10.08, -66.96) * mm, v(-10.12, -68.3) * mm, v(-10.17, -69.4) * mm, v(-10.25, -70.28) * mm]});
            skFitSpline(sketch, "E571", {"points": [v(-10.25, -70.28) * mm, v(-9.37, -70.2) * mm, v(-8.52, -70.16) * mm, v(-7.68, -70.16) * mm]});
            skFitSpline(sketch, "E572", {"points": [v(-7.68, -70.16) * mm, v(-6.84, -70.16) * mm, v(-5.98, -70.2) * mm, v(-5.1, -70.28) * mm]});
            skFitSpline(sketch, "E573", {"points": [v(-5.1, -70.28) * mm, v(-5.18, -69.4) * mm, v(-5.26, -68.3) * mm, v(-5.34, -66.96) * mm]});
            skFitSpline(sketch, "E574", {"points": [v(-5.34, -66.96) * mm, v(-5.37, -65.63) * mm, v(-5.41, -64.22) * mm, v(-5.45, -62.74) * mm]});
            skFitSpline(sketch, "E575", {"points": [v(-5.45, -62.74) * mm, v(-5.49, -61.25) * mm, v(-5.53, -59.75) * mm, v(-5.57, -58.22) * mm]});
            skFitSpline(sketch, "E576", {"points": [v(-5.57, -58.22) * mm, v(-5.57, -56.7) * mm, v(-5.57, -55.29) * mm, v(-5.57, -54) * mm]});
            skLineSegment(sketch, "E577", {"start": v(-9.8, -43.65) * mm, "end": v(-9.8, -54) * mm});
            skLineSegment(sketch, "E578", {"start": v(-9.8, -54) * mm, "end": v(-9.8, -43.65) * mm});
            skFitSpline(sketch, "E579", {"points": [v(-5.57, -43.65) * mm, v(-5.57, -42.35) * mm, v(-5.57, -40.95) * mm, v(-5.57, -39.42) * mm]});
            skFitSpline(sketch, "E580", {"points": [v(-5.57, -39.42) * mm, v(-5.53, -37.9) * mm, v(-5.49, -36.4) * mm, v(-5.45, -34.9) * mm]});
            skFitSpline(sketch, "E581", {"points": [v(-5.45, -34.9) * mm, v(-5.41, -33.42) * mm, v(-5.37, -32.01) * mm, v(-5.34, -30.68) * mm]});
            skFitSpline(sketch, "E582", {"points": [v(-5.34, -30.68) * mm, v(-5.26, -29.3) * mm, v(-5.18, -28.15) * mm, v(-5.1, -27.2) * mm]});
            skFitSpline(sketch, "E583", {"points": [v(-5.1, -27.2) * mm, v(-6.17, -27.38) * mm, v(-7.03, -27.48) * mm, v(-7.68, -27.48) * mm]});
            skFitSpline(sketch, "E584", {"points": [v(-7.68, -27.48) * mm, v(-8.33, -27.48) * mm, v(-9.18, -27.38) * mm, v(-10.25, -27.2) * mm]});
            skFitSpline(sketch, "E585", {"points": [v(-10.25, -27.2) * mm, v(-10.17, -28.15) * mm, v(-10.12, -29.3) * mm, v(-10.08, -30.68) * mm]});
            skFitSpline(sketch, "E586", {"points": [v(-10.08, -30.68) * mm, v(-10, -32.01) * mm, v(-9.95, -33.42) * mm, v(-9.9, -34.9) * mm]});
            skFitSpline(sketch, "E587", {"points": [v(-9.9, -34.9) * mm, v(-9.87, -36.4) * mm, v(-9.85, -37.9) * mm, v(-9.85, -39.42) * mm]});
            skFitSpline(sketch, "E588", {"points": [v(-9.85, -39.42) * mm, v(-9.81, -40.95) * mm, v(-9.8, -42.35) * mm, v(-9.8, -43.65) * mm]});
            skLineSegment(sketch, "E589", {"start": v(-5.57, -54) * mm, "end": v(-5.57, -43.65) * mm});
            skLineSegment(sketch, "E590", {"start": v(-5.57, -43.65) * mm, "end": v(-5.57, -54) * mm});
            skFitSpline(sketch, "E591", {"points": [v(5.37, -33.2) * mm, v(5.37, -34) * mm, v(5.65, -34.68) * mm, v(6.22, -35.25) * mm]});
            skFitSpline(sketch, "E592", {"points": [v(6.22, -35.25) * mm, v(6.8, -35.82) * mm, v(7.48, -36.1) * mm, v(8.28, -36.1) * mm]});
            skFitSpline(sketch, "E593", {"points": [v(8.28, -36.1) * mm, v(9.08, -36.1) * mm, v(9.77, -35.82) * mm, v(10.34, -35.25) * mm]});
            skFitSpline(sketch, "E594", {"points": [v(10.34, -35.25) * mm, v(10.9, -34.68) * mm, v(11.2, -34) * mm, v(11.2, -33.2) * mm]});
            skFitSpline(sketch, "E595", {"points": [v(11.2, -33.2) * mm, v(11.2, -32.4) * mm, v(10.9, -31.7) * mm, v(10.34, -31.14) * mm]});
            skFitSpline(sketch, "E596", {"points": [v(10.34, -31.14) * mm, v(9.77, -30.56) * mm, v(9.08, -30.28) * mm, v(8.28, -30.28) * mm]});
            skFitSpline(sketch, "E597", {"points": [v(8.28, -30.28) * mm, v(7.48, -30.28) * mm, v(6.8, -30.56) * mm, v(6.22, -31.14) * mm]});
            skFitSpline(sketch, "E598", {"points": [v(6.22, -31.14) * mm, v(5.65, -31.7) * mm, v(5.37, -32.4) * mm, v(5.37, -33.2) * mm]});
            skFitSpline(sketch, "E599", {"points": [v(6.17, -59.76) * mm, v(6.17, -61.48) * mm, v(6.13, -63.29) * mm, v(6.05, -65.2) * mm]});
            skFitSpline(sketch, "E600", {"points": [v(6.05, -65.2) * mm, v(6.01, -67.06) * mm, v(5.9, -68.75) * mm, v(5.7, -70.28) * mm]});
            skFitSpline(sketch, "E601", {"points": [v(5.7, -70.28) * mm, v(6.59, -70.2) * mm, v(7.44, -70.16) * mm, v(8.28, -70.16) * mm]});
            skFitSpline(sketch, "E602", {"points": [v(8.28, -70.16) * mm, v(9.12, -70.16) * mm, v(9.98, -70.2) * mm, v(10.85, -70.28) * mm]});
            skFitSpline(sketch, "E603", {"points": [v(10.85, -70.28) * mm, v(10.66, -68.75) * mm, v(10.53, -67.06) * mm, v(10.45, -65.2) * mm]});
            skFitSpline(sketch, "E604", {"points": [v(10.45, -65.2) * mm, v(10.41, -63.29) * mm, v(10.4, -61.48) * mm, v(10.4, -59.76) * mm]});
            skLineSegment(sketch, "E605", {"start": v(6.17, -53.82) * mm, "end": v(6.17, -59.76) * mm});
            skLineSegment(sketch, "E606", {"start": v(6.17, -59.76) * mm, "end": v(6.17, -53.82) * mm});
            skFitSpline(sketch, "E607", {"points": [v(10.4, -53.82) * mm, v(10.4, -52.1) * mm, v(10.41, -50.32) * mm, v(10.45, -48.45) * mm]});
            skFitSpline(sketch, "E608", {"points": [v(10.45, -48.45) * mm, v(10.53, -46.55) * mm, v(10.66, -44.77) * mm, v(10.85, -43.14) * mm]});
            skFitSpline(sketch, "E609", {"points": [v(10.85, -43.14) * mm, v(9.79, -43.33) * mm, v(8.93, -43.42) * mm, v(8.28, -43.42) * mm]});
            skFitSpline(sketch, "E610", {"points": [v(8.28, -43.42) * mm, v(7.63, -43.42) * mm, v(6.78, -43.33) * mm, v(5.7, -43.14) * mm]});
            skFitSpline(sketch, "E611", {"points": [v(5.7, -43.14) * mm, v(5.9, -44.77) * mm, v(6.01, -46.55) * mm, v(6.05, -48.45) * mm]});
            skFitSpline(sketch, "E612", {"points": [v(6.05, -48.45) * mm, v(6.13, -50.32) * mm, v(6.17, -52.1) * mm, v(6.17, -53.82) * mm]});
            skLineSegment(sketch, "E613", {"start": v(10.4, -59.76) * mm, "end": v(10.4, -53.82) * mm});
            skLineSegment(sketch, "E614", {"start": v(10.4, -53.82) * mm, "end": v(10.4, -59.76) * mm});
            skFitSpline(sketch, "E615", {"points": [v(39.16, -57.7) * mm, v(39.16, -59.92) * mm, v(39.1, -62.07) * mm, v(38.99, -64.16) * mm]});
            skFitSpline(sketch, "E616", {"points": [v(38.99, -64.16) * mm, v(38.9, -66.26) * mm, v(38.83, -68.3) * mm, v(38.76, -70.28) * mm]});
            skFitSpline(sketch, "E617", {"points": [v(38.76, -70.28) * mm, v(39.52, -70.2) * mm, v(40.3, -70.16) * mm, v(41.1, -70.16) * mm]});
            skFitSpline(sketch, "E618", {"points": [v(41.1, -70.16) * mm, v(41.94, -70.16) * mm, v(42.74, -70.2) * mm, v(43.5, -70.28) * mm]});
            skFitSpline(sketch, "E619", {"points": [v(43.5, -70.28) * mm, v(43.46, -69.75) * mm, v(43.42, -69.2) * mm, v(43.39, -68.62) * mm]});
            skFitSpline(sketch, "E620", {"points": [v(43.39, -68.62) * mm, v(43.39, -68.01) * mm, v(43.39, -67.4) * mm, v(43.39, -66.8) * mm]});
            skLineSegment(sketch, "E621", {"start": v(39.16, -54.22) * mm, "end": v(39.16, -57.7) * mm});
            skLineSegment(sketch, "E622", {"start": v(39.16, -57.7) * mm, "end": v(39.16, -54.22) * mm});
            skFitSpline(sketch, "E623", {"points": [v(43.39, -63.08) * mm, v(43.39, -61.14) * mm, v(43.42, -59.3) * mm, v(43.5, -57.6) * mm]});
            skFitSpline(sketch, "E624", {"points": [v(43.5, -57.6) * mm, v(43.58, -55.84) * mm, v(43.61, -54.15) * mm, v(43.61, -52.5) * mm]});
            skFitSpline(sketch, "E625", {"points": [v(43.61, -52.5) * mm, v(43.61, -50.53) * mm, v(43.33, -48.9) * mm, v(42.76, -47.65) * mm]});
            skFitSpline(sketch, "E626", {"points": [v(42.76, -47.65) * mm, v(42.22, -46.35) * mm, v(41.52, -45.35) * mm, v(40.64, -44.62) * mm]});
            skFitSpline(sketch, "E627", {"points": [v(40.64, -44.62) * mm, v(39.77, -43.86) * mm, v(38.78, -43.33) * mm, v(37.67, -43.02) * mm]});
            skFitSpline(sketch, "E628", {"points": [v(37.67, -43.02) * mm, v(36.6, -42.72) * mm, v(35.54, -42.56) * mm, v(34.47, -42.56) * mm]});
            skFitSpline(sketch, "E629", {"points": [v(34.47, -42.56) * mm, v(32.41, -42.56) * mm, v(30.64, -43.02) * mm, v(29.16, -43.94) * mm]});
            skFitSpline(sketch, "E630", {"points": [v(29.16, -43.94) * mm, v(27.67, -44.81) * mm, v(26.4, -46.07) * mm, v(25.33, -47.7) * mm]});
            skLineSegment(sketch, "E631", {"start": v(43.39, -66.8) * mm, "end": v(43.39, -63.08) * mm});
            skLineSegment(sketch, "E632", {"start": v(43.39, -63.08) * mm, "end": v(43.39, -66.8) * mm});
            skFitSpline(sketch, "E633", {"points": [v(25.21, -47.7) * mm, v(25.21, -46.18) * mm, v(25.27, -44.66) * mm, v(25.39, -43.14) * mm]});
            skFitSpline(sketch, "E634", {"points": [v(25.39, -43.14) * mm, v(24.9, -43.21) * mm, v(24.45, -43.29) * mm, v(24.07, -43.36) * mm]});
            skFitSpline(sketch, "E635", {"points": [v(24.07, -43.36) * mm, v(23.73, -43.4) * mm, v(23.4, -43.42) * mm, v(23.1, -43.42) * mm]});
            skFitSpline(sketch, "E636", {"points": [v(23.1, -43.42) * mm, v(22.45, -43.42) * mm, v(21.6, -43.33) * mm, v(20.53, -43.14) * mm]});
            skFitSpline(sketch, "E637", {"points": [v(20.53, -43.14) * mm, v(20.72, -44.77) * mm, v(20.83, -46.55) * mm, v(20.87, -48.45) * mm]});
            skFitSpline(sketch, "E638", {"points": [v(20.87, -48.45) * mm, v(20.95, -50.32) * mm, v(20.99, -52.1) * mm, v(20.99, -53.82) * mm]});
            skLineSegment(sketch, "E639", {"start": v(25.33, -47.7) * mm, "end": v(25.21, -47.7) * mm});
            skLineSegment(sketch, "E640", {"start": v(25.21, -47.7) * mm, "end": v(25.33, -47.7) * mm});
            skFitSpline(sketch, "E641", {"points": [v(20.99, -59.76) * mm, v(20.99, -61.48) * mm, v(20.95, -63.29) * mm, v(20.87, -65.2) * mm]});
            skFitSpline(sketch, "E642", {"points": [v(20.87, -65.2) * mm, v(20.83, -67.06) * mm, v(20.72, -68.75) * mm, v(20.53, -70.28) * mm]});
            skFitSpline(sketch, "E643", {"points": [v(20.53, -70.28) * mm, v(21.4, -70.2) * mm, v(22.26, -70.16) * mm, v(23.1, -70.16) * mm]});
            skFitSpline(sketch, "E644", {"points": [v(23.1, -70.16) * mm, v(23.94, -70.16) * mm, v(24.8, -70.2) * mm, v(25.67, -70.28) * mm]});
            skFitSpline(sketch, "E645", {"points": [v(25.67, -70.28) * mm, v(25.48, -68.75) * mm, v(25.35, -67.06) * mm, v(25.27, -65.2) * mm]});
            skFitSpline(sketch, "E646", {"points": [v(25.27, -65.2) * mm, v(25.23, -63.29) * mm, v(25.21, -61.48) * mm, v(25.21, -59.76) * mm]});
            skLineSegment(sketch, "E647", {"start": v(20.99, -53.82) * mm, "end": v(20.99, -59.76) * mm});
            skLineSegment(sketch, "E648", {"start": v(20.99, -59.76) * mm, "end": v(20.99, -53.82) * mm});
            skFitSpline(sketch, "E649", {"points": [v(25.21, -54.9) * mm, v(25.21, -51.94) * mm, v(25.82, -49.63) * mm, v(27.04, -48) * mm]});
            skFitSpline(sketch, "E650", {"points": [v(27.04, -48) * mm, v(28.3, -46.35) * mm, v(30.26, -45.54) * mm, v(32.93, -45.54) * mm]});
            skFitSpline(sketch, "E651", {"points": [v(32.93, -45.54) * mm, v(34.87, -45.54) * mm, v(36.4, -46.28) * mm, v(37.5, -47.76) * mm]});
            skFitSpline(sketch, "E652", {"points": [v(37.5, -47.76) * mm, v(38.6, -49.21) * mm, v(39.16, -51.36) * mm, v(39.16, -54.22) * mm]});
            skLineSegment(sketch, "E653", {"start": v(25.21, -59.76) * mm, "end": v(25.21, -54.9) * mm});
            skLineSegment(sketch, "E654", {"start": v(25.21, -54.9) * mm, "end": v(25.21, -59.76) * mm});
            skFitSpline(sketch, "E655", {"points": [v(71.14, -76.34) * mm, v(71.14, -77.63) * mm, v(70.87, -78.74) * mm, v(70.34, -79.65) * mm]});
            skFitSpline(sketch, "E656", {"points": [v(70.34, -79.65) * mm, v(69.8, -80.6) * mm, v(69.1, -81.38) * mm, v(68.22, -82) * mm]});
            skFitSpline(sketch, "E657", {"points": [v(68.22, -82) * mm, v(67.38, -82.6) * mm, v(66.41, -83.06) * mm, v(65.3, -83.36) * mm]});
            skFitSpline(sketch, "E658", {"points": [v(65.3, -83.36) * mm, v(64.2, -83.67) * mm, v(63.08, -83.82) * mm, v(61.94, -83.82) * mm]});
            skFitSpline(sketch, "E659", {"points": [v(61.94, -83.82) * mm, v(60.76, -83.82) * mm, v(59.65, -83.69) * mm, v(58.62, -83.42) * mm]});
            skFitSpline(sketch, "E660", {"points": [v(58.62, -83.42) * mm, v(57.6, -83.15) * mm, v(56.7, -82.74) * mm, v(55.94, -82.16) * mm]});
            skFitSpline(sketch, "E661", {"points": [v(55.94, -82.16) * mm, v(55.21, -81.6) * mm, v(54.62, -80.85) * mm, v(54.17, -79.94) * mm]});
            skFitSpline(sketch, "E662", {"points": [v(54.17, -79.94) * mm, v(53.75, -79.02) * mm, v(53.54, -77.92) * mm, v(53.54, -76.62) * mm]});
            skFitSpline(sketch, "E663", {"points": [v(53.54, -76.62) * mm, v(53.54, -74.18) * mm, v(54.32, -72.49) * mm, v(55.88, -71.54) * mm]});
            skFitSpline(sketch, "E664", {"points": [v(55.88, -71.54) * mm, v(57.44, -70.62) * mm, v(59.65, -70.16) * mm, v(62.5, -70.16) * mm]});
            skFitSpline(sketch, "E665", {"points": [v(62.5, -70.16) * mm, v(65.6, -70.16) * mm, v(67.8, -70.62) * mm, v(69.14, -71.54) * mm]});
            skFitSpline(sketch, "E666", {"points": [v(69.14, -71.54) * mm, v(70.47, -72.45) * mm, v(71.14, -74.05) * mm, v(71.14, -76.34) * mm]});
            skFitSpline(sketch, "E667", {"points": [v(68.05, -51.6) * mm, v(68.05, -52.66) * mm, v(67.92, -53.69) * mm, v(67.65, -54.68) * mm]});
            skFitSpline(sketch, "E668", {"points": [v(67.65, -54.68) * mm, v(67.42, -55.63) * mm, v(67.04, -56.49) * mm, v(66.5, -57.25) * mm]});
            skFitSpline(sketch, "E669", {"points": [v(66.5, -57.25) * mm, v(66.01, -57.97) * mm, v(65.37, -58.56) * mm, v(64.57, -59.02) * mm]});
            skFitSpline(sketch, "E670", {"points": [v(64.57, -59.02) * mm, v(63.8, -59.44) * mm, v(62.87, -59.65) * mm, v(61.77, -59.65) * mm]});
            skFitSpline(sketch, "E671", {"points": [v(61.77, -59.65) * mm, v(59.56, -59.65) * mm, v(57.92, -58.96) * mm, v(56.85, -57.6) * mm]});
            skFitSpline(sketch, "E672", {"points": [v(56.85, -57.6) * mm, v(55.82, -56.18) * mm, v(55.3, -54.28) * mm, v(55.3, -51.88) * mm]});
            skFitSpline(sketch, "E673", {"points": [v(55.3, -51.88) * mm, v(55.3, -49.55) * mm, v(55.88, -47.7) * mm, v(57.02, -46.34) * mm]});
            skFitSpline(sketch, "E674", {"points": [v(57.02, -46.34) * mm, v(58.17, -44.93) * mm, v(59.77, -44.22) * mm, v(61.82, -44.22) * mm]});
            skFitSpline(sketch, "E675", {"points": [v(61.82, -44.22) * mm, v(63.69, -44.22) * mm, v(65.2, -44.85) * mm, v(66.34, -46.1) * mm]});
            skFitSpline(sketch, "E676", {"points": [v(66.34, -46.1) * mm, v(67.48, -47.36) * mm, v(68.05, -49.2) * mm, v(68.05, -51.6) * mm]});
            skFitSpline(sketch, "E677", {"points": [v(50.85, -51.88) * mm, v(50.85, -53.97) * mm, v(51.35, -55.73) * mm, v(52.34, -57.14) * mm]});
            skFitSpline(sketch, "E678", {"points": [v(52.34, -57.14) * mm, v(53.33, -58.5) * mm, v(54.7, -59.57) * mm, v(56.45, -60.34) * mm]});
            skFitSpline(sketch, "E679", {"points": [v(56.45, -60.45) * mm, v(56, -60.53) * mm, v(55.52, -60.7) * mm, v(55.02, -60.96) * mm]});
            skFitSpline(sketch, "E680", {"points": [v(55.02, -60.96) * mm, v(54.53, -61.23) * mm, v(54.09, -61.57) * mm, v(53.7, -62) * mm]});
            skFitSpline(sketch, "E681", {"points": [v(53.7, -62) * mm, v(53.33, -62.41) * mm, v(53, -62.89) * mm, v(52.74, -63.42) * mm]});
            skFitSpline(sketch, "E682", {"points": [v(52.74, -63.42) * mm, v(52.5, -63.95) * mm, v(52.4, -64.55) * mm, v(52.4, -65.2) * mm]});
            skFitSpline(sketch, "E683", {"points": [v(52.4, -65.2) * mm, v(52.4, -66.3) * mm, v(52.7, -67.25) * mm, v(53.3, -68.05) * mm]});
            skFitSpline(sketch, "E684", {"points": [v(53.3, -68.05) * mm, v(53.92, -68.85) * mm, v(54.81, -69.42) * mm, v(56, -69.76) * mm]});
            skLineSegment(sketch, "E685", {"start": v(56.45, -60.34) * mm, "end": v(56.45, -60.45) * mm});
            skLineSegment(sketch, "E686", {"start": v(56.45, -60.45) * mm, "end": v(56.45, -60.34) * mm});
            skFitSpline(sketch, "E687", {"points": [v(56, -69.88) * mm, v(55.23, -70.07) * mm, v(54.49, -70.35) * mm, v(53.77, -70.74) * mm]});
            skFitSpline(sketch, "E688", {"points": [v(53.77, -70.74) * mm, v(53.04, -71.12) * mm, v(52.4, -71.63) * mm, v(51.82, -72.28) * mm]});
            skFitSpline(sketch, "E689", {"points": [v(51.82, -72.28) * mm, v(51.25, -72.93) * mm, v(50.77, -73.67) * mm, v(50.4, -74.5) * mm]});
            skFitSpline(sketch, "E690", {"points": [v(50.4, -74.5) * mm, v(50.05, -75.35) * mm, v(49.88, -76.26) * mm, v(49.88, -77.25) * mm]});
            skFitSpline(sketch, "E691", {"points": [v(49.88, -77.25) * mm, v(49.88, -79.8) * mm, v(50.95, -81.8) * mm, v(53.08, -83.25) * mm]});
            skFitSpline(sketch, "E692", {"points": [v(53.08, -83.25) * mm, v(55.21, -84.74) * mm, v(58.13, -85.48) * mm, v(61.82, -85.48) * mm]});
            skFitSpline(sketch, "E693", {"points": [v(61.82, -85.48) * mm, v(64.22, -85.48) * mm, v(66.28, -85.12) * mm, v(68, -84.4) * mm]});
            skFitSpline(sketch, "E694", {"points": [v(68, -84.4) * mm, v(69.7, -83.67) * mm, v(71.1, -82.75) * mm, v(72.17, -81.65) * mm]});
            skFitSpline(sketch, "E695", {"points": [v(72.17, -81.65) * mm, v(73.27, -80.55) * mm, v(74.07, -79.3) * mm, v(74.57, -77.94) * mm]});
            skFitSpline(sketch, "E696", {"points": [v(74.57, -77.94) * mm, v(75.1, -76.56) * mm, v(75.37, -75.21) * mm, v(75.37, -73.88) * mm]});
            skFitSpline(sketch, "E697", {"points": [v(75.37, -73.88) * mm, v(75.37, -72.89) * mm, v(75.17, -71.97) * mm, v(74.8, -71.14) * mm]});
            skFitSpline(sketch, "E698", {"points": [v(74.8, -71.14) * mm, v(74.45, -70.3) * mm, v(73.88, -69.55) * mm, v(73.08, -68.9) * mm]});
            skFitSpline(sketch, "E699", {"points": [v(73.08, -68.9) * mm, v(72.32, -68.26) * mm, v(71.3, -67.75) * mm, v(70.05, -67.36) * mm]});
            skFitSpline(sketch, "E700", {"points": [v(70.05, -67.36) * mm, v(68.83, -66.98) * mm, v(67.35, -66.77) * mm, v(65.6, -66.74) * mm]});
            skFitSpline(sketch, "E701", {"points": [v(65.6, -66.74) * mm, v(64.53, -66.7) * mm, v(63.48, -66.68) * mm, v(62.45, -66.68) * mm]});
            skFitSpline(sketch, "E702", {"points": [v(62.45, -66.68) * mm, v(61.42, -66.64) * mm, v(60.37, -66.6) * mm, v(59.3, -66.56) * mm]});
            skFitSpline(sketch, "E703", {"points": [v(59.3, -66.56) * mm, v(58.01, -66.53) * mm, v(57.12, -66.28) * mm, v(56.62, -65.82) * mm]});
            skFitSpline(sketch, "E704", {"points": [v(56.62, -65.82) * mm, v(56.17, -65.36) * mm, v(55.94, -64.64) * mm, v(55.94, -63.65) * mm]});
            skFitSpline(sketch, "E705", {"points": [v(55.94, -63.65) * mm, v(55.94, -62.89) * mm, v(56.22, -62.26) * mm, v(56.8, -61.76) * mm]});
            skFitSpline(sketch, "E706", {"points": [v(56.8, -61.76) * mm, v(57.4, -61.27) * mm, v(58.05, -61.02) * mm, v(58.74, -61.02) * mm]});
            skFitSpline(sketch, "E707", {"points": [v(58.74, -61.02) * mm, v(59.27, -61.02) * mm, v(59.78, -61.04) * mm, v(60.28, -61.08) * mm]});
            skFitSpline(sketch, "E708", {"points": [v(60.28, -61.08) * mm, v(60.81, -61.12) * mm, v(61.35, -61.14) * mm, v(61.88, -61.14) * mm]});
            skFitSpline(sketch, "E709", {"points": [v(61.88, -61.14) * mm, v(65.12, -61.14) * mm, v(67.69, -60.34) * mm, v(69.6, -58.74) * mm]});
            skFitSpline(sketch, "E710", {"points": [v(69.6, -58.74) * mm, v(71.54, -57.1) * mm, v(72.5, -54.85) * mm, v(72.5, -52) * mm]});
            skFitSpline(sketch, "E711", {"points": [v(72.5, -52) * mm, v(72.5, -50.55) * mm, v(72.15, -49.15) * mm, v(71.42, -47.82) * mm]});
            skFitSpline(sketch, "E712", {"points": [v(71.42, -47.82) * mm, v(70.7, -46.45) * mm, v(69.75, -45.44) * mm, v(68.57, -44.8) * mm]});
            skLineSegment(sketch, "E713", {"start": v(56, -69.76) * mm, "end": v(56, -69.88) * mm});
            skLineSegment(sketch, "E714", {"start": v(56, -69.88) * mm, "end": v(56, -69.76) * mm});
            skFitSpline(sketch, "E715", {"points": [v(68.68, -44.68) * mm, v(69.7, -44.72) * mm, v(70.74, -44.8) * mm, v(71.77, -44.9) * mm]});
            skFitSpline(sketch, "E716", {"points": [v(71.77, -44.9) * mm, v(72.83, -44.98) * mm, v(73.92, -45.06) * mm, v(75.02, -45.14) * mm]});
            skFitSpline(sketch, "E717", {"points": [v(75.02, -45.14) * mm, v(74.98, -44.95) * mm, v(74.95, -44.75) * mm, v(74.9, -44.56) * mm]});
            skFitSpline(sketch, "E718", {"points": [v(74.9, -44.56) * mm, v(74.9, -44.34) * mm, v(74.9, -44.13) * mm, v(74.9, -43.94) * mm]});
            skFitSpline(sketch, "E719", {"points": [v(74.9, -43.94) * mm, v(74.9, -43.75) * mm, v(74.9, -43.55) * mm, v(74.9, -43.36) * mm]});
            skFitSpline(sketch, "E720", {"points": [v(74.9, -43.36) * mm, v(74.95, -43.14) * mm, v(74.98, -42.93) * mm, v(75.02, -42.74) * mm]});
            skFitSpline(sketch, "E721", {"points": [v(75.02, -42.74) * mm, v(74.07, -42.93) * mm, v(72.53, -43.02) * mm, v(70.4, -43.02) * mm]});
            skFitSpline(sketch, "E722", {"points": [v(70.4, -43.02) * mm, v(69.97, -43.02) * mm, v(69.42, -43) * mm, v(68.74, -42.96) * mm]});
            skFitSpline(sketch, "E723", {"points": [v(68.74, -42.96) * mm, v(68.05, -42.93) * mm, v(67.27, -42.87) * mm, v(66.4, -42.8) * mm]});
            skFitSpline(sketch, "E724", {"points": [v(66.4, -42.8) * mm, v(65.37, -42.72) * mm, v(64.5, -42.66) * mm, v(63.82, -42.62) * mm]});
            skFitSpline(sketch, "E725", {"points": [v(63.82, -42.62) * mm, v(63.17, -42.58) * mm, v(62.49, -42.56) * mm, v(61.77, -42.56) * mm]});
            skFitSpline(sketch, "E726", {"points": [v(61.77, -42.56) * mm, v(60.28, -42.56) * mm, v(58.87, -42.75) * mm, v(57.54, -43.14) * mm]});
            skFitSpline(sketch, "E727", {"points": [v(57.54, -43.14) * mm, v(56.24, -43.52) * mm, v(55.08, -44.09) * mm, v(54.05, -44.85) * mm]});
            skFitSpline(sketch, "E728", {"points": [v(54.05, -44.85) * mm, v(53.06, -45.61) * mm, v(52.28, -46.58) * mm, v(51.7, -47.76) * mm]});
            skFitSpline(sketch, "E729", {"points": [v(51.7, -47.76) * mm, v(51.14, -48.9) * mm, v(50.85, -50.28) * mm, v(50.85, -51.88) * mm]});
            skLineSegment(sketch, "E730", {"start": v(68.57, -44.8) * mm, "end": v(68.68, -44.68) * mm});
            skLineSegment(sketch, "E731", {"start": v(68.68, -44.68) * mm, "end": v(68.57, -44.8) * mm});
            skPoint(sketch, "E732.middle", {"position": v(0, 0) * mm});
            skSolve(sketch);
        }
        {
            var Q0;
            Q0=makeQuery(id+"F0.imprint","IMPRINT",FACE,{"disambiguationData":[TD([[makeQuery(id+"F0.imprint","IMPRINT",EDGE,{"derivedFrom":sQuery(id+"F0.wireOp",EDGE,"E0")}),-1.0]])]});
            var Q1;
            Q1=makeQuery(id+"F0.imprint","IMPRINT",FACE,{"disambiguationData":[TD([[makeQuery(id+"F0.imprint","IMPRINT",EDGE,{"derivedFrom":sQuery(id+"F0.wireOp",EDGE,"E33")}),1.0]])]});
            var Q2;
            Q2=makeQuery(id+"F0.imprint","IMPRINT",FACE,{"disambiguationData":[TD([[makeQuery(id+"F0.imprint","IMPRINT",EDGE,{"derivedFrom":sQuery(id+"F0.wireOp",EDGE,"E73")}),1.0]])]});
            var Q3;
            Q3=makeQuery(id+"F0.imprint","IMPRINT",FACE,{"disambiguationData":[TD([[makeQuery(id+"F0.imprint","IMPRINT",EDGE,{"derivedFrom":sQuery(id+"F0.wireOp",EDGE,"E127")}),1.0]])]});
            var Q4;
            Q4=makeQuery(id+"F0.imprint","IMPRINT",FACE,{"disambiguationData":[TD([[makeQuery(id+"F0.imprint","IMPRINT",EDGE,{"derivedFrom":sQuery(id+"F0.wireOp",EDGE,"E119")}),1.0]])]});
            var Q5;
            Q5=makeQuery(id+"F0.imprint","IMPRINT",FACE,{"disambiguationData":[TD([[makeQuery(id+"F0.imprint","IMPRINT",EDGE,{"derivedFrom":sQuery(id+"F0.wireOp",EDGE,"E143")}),1.0]])]});
            var Q6;
            Q6=makeQuery(id+"F0.imprint","IMPRINT",FACE,{"disambiguationData":[TD([[makeQuery(id+"F0.imprint","IMPRINT",EDGE,{"derivedFrom":sQuery(id+"F0.wireOp",EDGE,"E192")}),1.0]])]});
            var Q7;
            Q7=makeQuery(id+"F0.imprint","IMPRINT",FACE,{"disambiguationData":[TD([[makeQuery(id+"F0.imprint","IMPRINT",EDGE,{"derivedFrom":sQuery(id+"F0.wireOp",EDGE,"E286")}),1.0]])]});
            var Q8;
            Q8=makeQuery(id+"F0.imprint","IMPRINT",FACE,{"disambiguationData":[TD([[makeQuery(id+"F0.imprint","IMPRINT",EDGE,{"derivedFrom":sQuery(id+"F0.wireOp",EDGE,"E333")}),1.0]])]});
            var Q9;
            Q9=makeQuery(id+"F0.imprint","IMPRINT",FACE,{"disambiguationData":[TD([[makeQuery(id+"F0.imprint","IMPRINT",EDGE,{"derivedFrom":sQuery(id+"F0.wireOp",EDGE,"E377")}),1.0]])]});
            var Q10;
            Q10=makeQuery(id+"F0.imprint","IMPRINT",FACE,{"disambiguationData":[TD([[makeQuery(id+"F0.imprint","IMPRINT",EDGE,{"derivedFrom":sQuery(id+"F0.wireOp",EDGE,"E424")}),1.0]])]});
            var Q11;
            Q11=makeQuery(id+"F0.imprint","IMPRINT",FACE,{"disambiguationData":[TD([[makeQuery(id+"F0.imprint","IMPRINT",EDGE,{"derivedFrom":sQuery(id+"F0.wireOp",EDGE,"E477")}),1.0]])]});
            var Q12;
            Q12=makeQuery(id+"F0.imprint","IMPRINT",FACE,{"disambiguationData":[TD([[makeQuery(id+"F0.imprint","IMPRINT",EDGE,{"derivedFrom":sQuery(id+"F0.wireOp",EDGE,"E240")}),1.0]])]});
            var Q13;
            Q13=makeQuery(id+"F0.imprint","IMPRINT",FACE,{"disambiguationData":[TD([[makeQuery(id+"F0.imprint","IMPRINT",EDGE,{"derivedFrom":sQuery(id+"F0.wireOp",EDGE,"E517")}),1.0]])]});
            var Q14;
            Q14=makeQuery(id+"F0.imprint","IMPRINT",FACE,{"disambiguationData":[TD([[makeQuery(id+"F0.imprint","IMPRINT",EDGE,{"derivedFrom":sQuery(id+"F0.wireOp",EDGE,"E567")}),1.0]])]});
            var Q15;
            Q15=makeQuery(id+"F0.imprint","IMPRINT",FACE,{"disambiguationData":[TD([[makeQuery(id+"F0.imprint","IMPRINT",EDGE,{"derivedFrom":sQuery(id+"F0.wireOp",EDGE,"E599")}),1.0]])]});
            var Q16;
            Q16=makeQuery(id+"F0.imprint","IMPRINT",FACE,{"disambiguationData":[TD([[makeQuery(id+"F0.imprint","IMPRINT",EDGE,{"derivedFrom":sQuery(id+"F0.wireOp",EDGE,"E615")}),1.0]])]});
            var Q17;
            Q17=makeQuery(id+"F0.imprint","IMPRINT",FACE,{"disambiguationData":[TD([[makeQuery(id+"F0.imprint","IMPRINT",EDGE,{"derivedFrom":sQuery(id+"F0.wireOp",EDGE,"E591")}),1.0]])]});
            var Q18;
            Q18=makeQuery(id+"F0.imprint","IMPRINT",FACE,{"disambiguationData":[TD([[makeQuery(id+"F0.imprint","IMPRINT",EDGE,{"derivedFrom":sQuery(id+"F0.wireOp",EDGE,"E655")}),1.0]])]});
            extrude(context, id + "F1", {"entities" : qUnion([Q0, Q1, Q2, Q3, Q4, Q5, Q6, Q7, Q8, Q9, Q10, Q11, Q12, Q13, Q14, Q15, Q16, Q17, Q18]), "depth" : 2 * mm, "offsetDistance" : 25 * mm});
        }
    });
